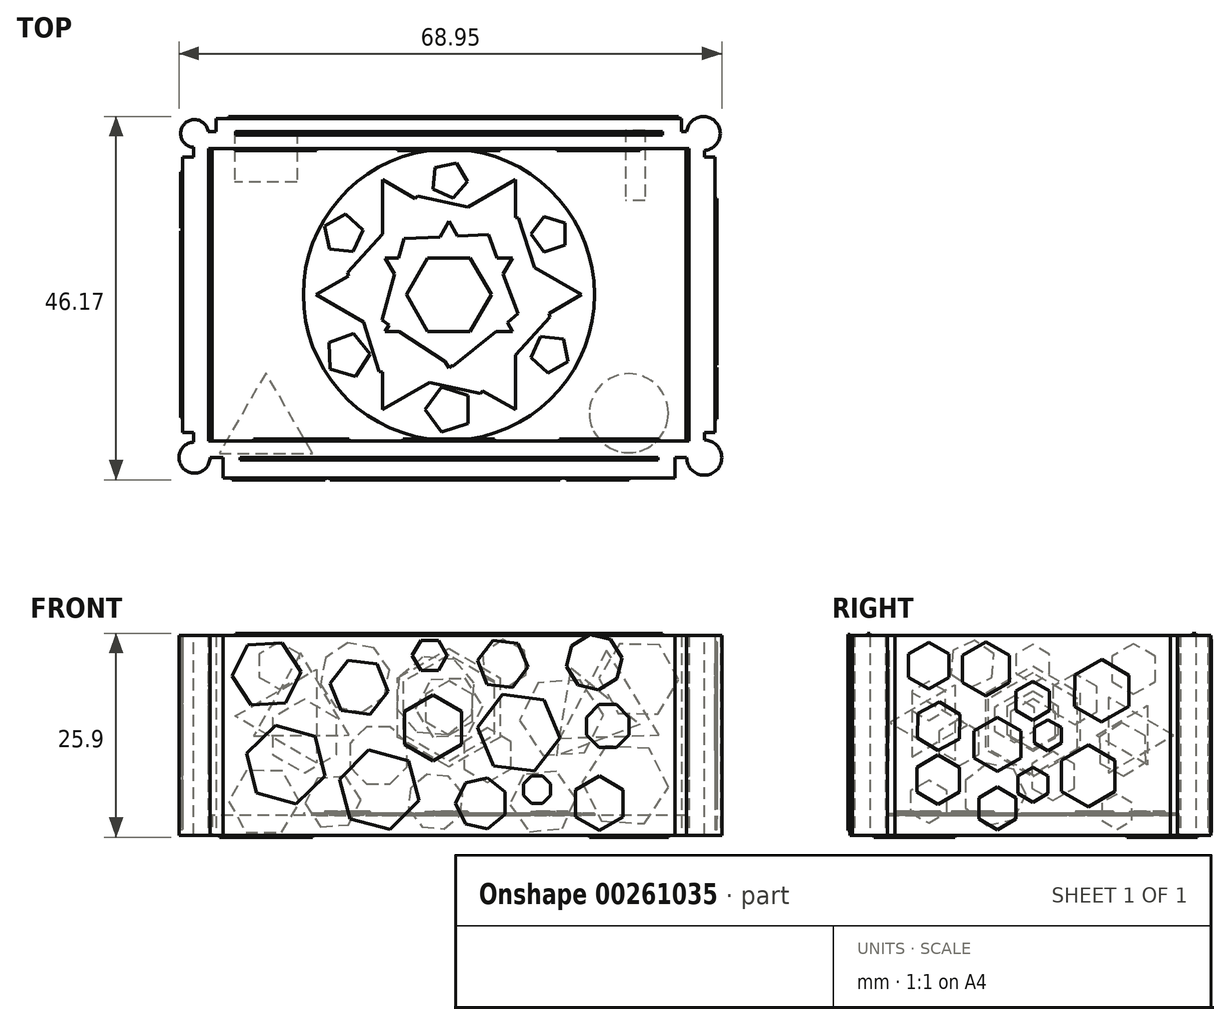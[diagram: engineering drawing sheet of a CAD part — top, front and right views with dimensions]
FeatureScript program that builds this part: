
annotation { "Feature Type Name" : "Feature", "Feature Type Description" : "" }
export const myFeature = defineFeature(function(context is Context, id is Id, definition is map)
    precondition{}
    {
        {
            var Q0;
            Q0=qCreatedBy(makeId("Top.planeOp"),FACE);
            var sketch = newSketch(context, id + "F0", { "sketchPlane" : qUnion([Q0])});
            skLineSegment(sketch, "E0.bottom", {"start": v(32.43, -20.7) * mm, "end": v(-32.43, -20.7) * mm});
            skLineSegment(sketch, "E0.top", {"start": v(32.43, 20.7) * mm, "end": v(-32.43, 20.7) * mm});
            skLineSegment(sketch, "E0.left", {"start": v(32.43, -20.7) * mm, "end": v(32.43, 20.7) * mm});
            skLineSegment(sketch, "E0.right", {"start": v(-32.43, -20.7) * mm, "end": v(-32.43, 20.7) * mm});
            skPoint(sketch, "E0.middle", {"position": v(0, 0) * mm});
            skLineSegment(sketch, "E1.bottom", {"start": v(30.51, -18.56) * mm, "end": v(-30.51, -18.56) * mm});
            skLineSegment(sketch, "E1.top", {"start": v(30.51, 18.56) * mm, "end": v(-30.51, 18.56) * mm});
            skLineSegment(sketch, "E1.left", {"start": v(30.51, -18.56) * mm, "end": v(30.51, 18.56) * mm});
            skLineSegment(sketch, "E1.right", {"start": v(-30.51, -18.56) * mm, "end": v(-30.51, 18.56) * mm});
            skSolve(sketch);
        }
        {
            var Q0;
            Q0=makeQuery(id+"F0.imprint","IMPRINT",FACE,{"disambiguationData":[TD([[makeQuery(id+"F0.imprint","IMPRINT",EDGE,{"derivedFrom":sQuery(id+"F0.wireOp",EDGE,"E0.bottom")}),-1.0]])]});
            extrude(context, id + "F1", {"entities" : qUnion([Q0]), "depth" : 25.4 * mm});
        }
        {
            var Q0;
            Q0=qCreatedBy(makeId("Top.planeOp"),FACE);
            var sketch = newSketch(context, id + "F2", { "sketchPlane" : qUnion([Q0])});
            skLineSegment(sketch, "E2.bottom", {"start": v(30.08, 18.56) * mm, "end": v(-30.08, 18.56) * mm});
            skLineSegment(sketch, "E2.top", {"start": v(30.08, -18.56) * mm, "end": v(-30.08, -18.56) * mm});
            skLineSegment(sketch, "E2.left", {"start": v(30.08, 18.56) * mm, "end": v(30.08, -18.56) * mm});
            skLineSegment(sketch, "E2.right", {"start": v(-30.08, 18.56) * mm, "end": v(-30.08, -18.56) * mm});
            skPoint(sketch, "E2.middle", {"position": v(0, 0) * mm});
            skSolve(sketch);
        }
        {
            var Q0;
            Q0=makeQuery(id+"F2.imprint","IMPRINT",FACE,{"disambiguationData":[TD([[makeQuery(id+"F2.imprint","IMPRINT",EDGE,{"derivedFrom":sQuery(id+"F2.wireOp",EDGE,"E2.bottom")}),1.0]])]});
            extrude(context, id + "F3", {"entities" : qUnion([Q0]), "operationType" : NewBodyOperationType.ADD, "depth" : 2.54 * mm});
        }
        {
            var Q0;
            Q0=qCreatedBy(makeId("Top.planeOp"),FACE);
            var sketch = newSketch(context, id + "F4", { "sketchPlane" : qUnion([Q0])});
            skCircle(sketch, "E3", {"center": v(32.43, -20.7) * mm, "radius": 2.23 * mm});
            skCircle(sketch, "E4", {"center": v(32.32, 20.48) * mm, "radius": 2.14 * mm});
            skCircle(sketch, "E5", {"center": v(-32.32, 20.48) * mm, "radius": 1.76 * mm});
            skCircle(sketch, "E6", {"center": v(-32.32, -20.7) * mm, "radius": 1.97 * mm});
            skSolve(sketch);
        }
        {
            var Q0;
            Q0 = qSketchRegion(id + "F4", true);
            extrude(context, id + "F5", {"entities" : qUnion([Q0]), "operationType" : NewBodyOperationType.ADD, "depth" : 25.4 * mm});
        }
        {
            var Q0;
            Q0=qCreatedBy(makeId("Top.planeOp"),FACE);
            var sketch = newSketch(context, id + "F6", { "sketchPlane" : qUnion([Q0])});
            skLineSegment(sketch, "E7.bottom", {"start": v(28.7, -23.26) * mm, "end": v(-28.7, -23.26) * mm});
            skLineSegment(sketch, "E7.top", {"start": v(28.7, -19.84) * mm, "end": v(-28.7, -19.84) * mm});
            skLineSegment(sketch, "E7.left", {"start": v(28.7, -23.26) * mm, "end": v(28.7, -19.84) * mm});
            skLineSegment(sketch, "E7.right", {"start": v(-28.7, -23.26) * mm, "end": v(-28.7, -19.84) * mm});
            skPoint(sketch, "E7.middle", {"position": v(0, -21.55) * mm});
            skLineSegment(sketch, "E8.bottom", {"start": v(29.55, 18.99) * mm, "end": v(-29.55, 18.99) * mm});
            skLineSegment(sketch, "E8.top", {"start": v(29.55, 22.4) * mm, "end": v(-29.55, 22.4) * mm});
            skLineSegment(sketch, "E8.left", {"start": v(29.55, 18.99) * mm, "end": v(29.55, 22.4) * mm});
            skLineSegment(sketch, "E8.right", {"start": v(-29.55, 18.99) * mm, "end": v(-29.55, 22.4) * mm});
            skPoint(sketch, "E8.middle", {"position": v(0, 20.7) * mm});
            skLineSegment(sketch, "E9.bottom", {"start": v(-31.26, -17.5) * mm, "end": v(-33.82, -17.5) * mm});
            skLineSegment(sketch, "E9.top", {"start": v(-31.26, 17.5) * mm, "end": v(-33.82, 17.5) * mm});
            skLineSegment(sketch, "E9.left", {"start": v(-31.26, -17.5) * mm, "end": v(-31.26, 17.5) * mm});
            skLineSegment(sketch, "E9.right", {"start": v(-33.82, -17.5) * mm, "end": v(-33.82, 17.5) * mm});
            skPoint(sketch, "E9.middle", {"position": v(-32.54, 0) * mm});
            skLineSegment(sketch, "E10.bottom", {"start": v(33.82, -17.5) * mm, "end": v(31.26, -17.5) * mm});
            skLineSegment(sketch, "E10.top", {"start": v(33.82, 17.5) * mm, "end": v(31.26, 17.5) * mm});
            skLineSegment(sketch, "E10.left", {"start": v(33.82, -17.5) * mm, "end": v(33.82, 17.5) * mm});
            skLineSegment(sketch, "E10.right", {"start": v(31.26, -17.5) * mm, "end": v(31.26, 17.5) * mm});
            skPoint(sketch, "E10.middle", {"position": v(32.54, 0) * mm});
            skSolve(sketch);
        }
        {
            var Q0;
            Q0 = qSketchRegion(id + "F6", true);
            extrude(context, id + "F7", {"entities" : qUnion([Q0]), "operationType" : NewBodyOperationType.ADD, "depth" : 25.4 * mm});
        }
        {
            var Q0;
            Q0=makeQuery(id+"F7.opExtrude","SWEPT_FACE",FACE,{"disambiguationData":[OSD([sQuery(id+"F6.wireOp",EDGE,"E7.bottom")])]});
            var sketch = newSketch(context, id + "F8", { "sketchPlane" : qUnion([Q0])});
            skCircle(sketch, "E11.cCircle", {"center": v(-23.15, 20.48) * mm, "radius": 3.82 * mm, "construction": true});
            skLineSegment(sketch, "E11.0", {"start": v(-18.75, 20.75) * mm, "end": v(-20.72, 16.8) * mm});
            skLineSegment(sketch, "E11.1", {"start": v(-20.72, 16.8) * mm, "end": v(-25.12, 16.54) * mm});
            skLineSegment(sketch, "E11.2", {"start": v(-25.12, 16.54) * mm, "end": v(-27.55, 20.22) * mm});
            skLineSegment(sketch, "E11.3", {"start": v(-27.55, 20.22) * mm, "end": v(-25.58, 24.16) * mm});
            skLineSegment(sketch, "E11.4", {"start": v(-25.58, 24.16) * mm, "end": v(-21.18, 24.42) * mm});
            skLineSegment(sketch, "E11.5", {"start": v(-21.18, 24.42) * mm, "end": v(-18.75, 20.75) * mm});
            skPoint(sketch, "E11.0.midPoint", {"position": v(-19.74, 18.78) * mm});
            skCircle(sketch, "E12.cCircle", {"center": v(-20.72, 8.96) * mm, "radius": 4.47 * mm, "construction": true});
            skLineSegment(sketch, "E12.0", {"start": v(-15.75, 7.56) * mm, "end": v(-19.45, 3.96) * mm});
            skLineSegment(sketch, "E12.1", {"start": v(-19.45, 3.96) * mm, "end": v(-24.42, 5.36) * mm});
            skLineSegment(sketch, "E12.2", {"start": v(-24.42, 5.36) * mm, "end": v(-25.69, 10.36) * mm});
            skLineSegment(sketch, "E12.3", {"start": v(-25.69, 10.36) * mm, "end": v(-22, 13.96) * mm});
            skLineSegment(sketch, "E12.4", {"start": v(-22, 13.96) * mm, "end": v(-17.03, 12.56) * mm});
            skLineSegment(sketch, "E12.5", {"start": v(-17.03, 12.56) * mm, "end": v(-15.75, 7.56) * mm});
            skPoint(sketch, "E12.0.midPoint", {"position": v(-17.6, 5.76) * mm});
            skCircle(sketch, "E13.cCircle", {"center": v(-11.41, 18.78) * mm, "radius": 3.23 * mm, "construction": true});
            skLineSegment(sketch, "E13.0", {"start": v(-7.72, 18.28) * mm, "end": v(-10, 15.33) * mm});
            skLineSegment(sketch, "E13.1", {"start": v(-10, 15.33) * mm, "end": v(-13.7, 15.82) * mm});
            skLineSegment(sketch, "E13.2", {"start": v(-13.7, 15.82) * mm, "end": v(-15.11, 19.27) * mm});
            skLineSegment(sketch, "E13.3", {"start": v(-15.11, 19.27) * mm, "end": v(-12.84, 22.22) * mm});
            skLineSegment(sketch, "E13.4", {"start": v(-12.84, 22.22) * mm, "end": v(-9.14, 21.73) * mm});
            skLineSegment(sketch, "E13.5", {"start": v(-9.14, 21.73) * mm, "end": v(-7.72, 18.28) * mm});
            skPoint(sketch, "E13.0.midPoint", {"position": v(-8.85, 16.8) * mm});
            skCircle(sketch, "E14.cCircle", {"center": v(-8.85, 5.76) * mm, "radius": 4.53 * mm, "construction": true});
            skLineSegment(sketch, "E14.0", {"start": v(-3.8, 4.4) * mm, "end": v(-7.5, 0.71) * mm});
            skLineSegment(sketch, "E14.1", {"start": v(-7.5, 0.71) * mm, "end": v(-12.55, 2.07) * mm});
            skLineSegment(sketch, "E14.2", {"start": v(-12.55, 2.07) * mm, "end": v(-13.9, 7.11) * mm});
            skLineSegment(sketch, "E14.3", {"start": v(-13.9, 7.11) * mm, "end": v(-10.2, 10.8) * mm});
            skLineSegment(sketch, "E14.4", {"start": v(-10.2, 10.8) * mm, "end": v(-5.16, 9.46) * mm});
            skLineSegment(sketch, "E14.5", {"start": v(-5.16, 9.46) * mm, "end": v(-3.8, 4.4) * mm});
            skPoint(sketch, "E14.0.midPoint", {"position": v(-5.65, 2.56) * mm});
            skCircle(sketch, "E15.cCircle", {"center": v(-2.03, 13.66) * mm, "radius": 3.63 * mm, "construction": true});
            skLineSegment(sketch, "E15.0", {"start": v(1.6, 15.75) * mm, "end": v(1.6, 11.56) * mm});
            skLineSegment(sketch, "E15.1", {"start": v(1.6, 11.56) * mm, "end": v(-2.03, 9.47) * mm});
            skLineSegment(sketch, "E15.2", {"start": v(-2.03, 9.47) * mm, "end": v(-5.65, 11.56) * mm});
            skLineSegment(sketch, "E15.3", {"start": v(-5.65, 11.56) * mm, "end": v(-5.65, 15.75) * mm});
            skLineSegment(sketch, "E15.4", {"start": v(-5.65, 15.75) * mm, "end": v(-2.03, 17.84) * mm});
            skLineSegment(sketch, "E15.5", {"start": v(-2.03, 17.84) * mm, "end": v(1.6, 15.75) * mm});
            skPoint(sketch, "E15.0.midPoint", {"position": v(1.6, 13.66) * mm});
            skCircle(sketch, "E16.cCircle", {"center": v(-2.45, 22.83) * mm, "radius": 1.92 * mm, "construction": true});
            skLineSegment(sketch, "E16.0", {"start": v(-1.34, 20.9) * mm, "end": v(-3.56, 20.9) * mm});
            skLineSegment(sketch, "E16.1", {"start": v(-3.56, 20.9) * mm, "end": v(-4.67, 22.83) * mm});
            skLineSegment(sketch, "E16.2", {"start": v(-4.67, 22.83) * mm, "end": v(-3.56, 24.75) * mm});
            skLineSegment(sketch, "E16.3", {"start": v(-3.56, 24.75) * mm, "end": v(-1.34, 24.75) * mm});
            skLineSegment(sketch, "E16.4", {"start": v(-1.34, 24.75) * mm, "end": v(-0.24, 22.83) * mm});
            skLineSegment(sketch, "E16.5", {"start": v(-0.24, 22.83) * mm, "end": v(-1.34, 20.9) * mm});
            skPoint(sketch, "E16.0.midPoint", {"position": v(-2.45, 20.9) * mm});
            skCircle(sketch, "E17.cCircle", {"center": v(4.16, 4.05) * mm, "radius": 2.99 * mm, "construction": true});
            skLineSegment(sketch, "E17.0", {"start": v(7.15, 5.5) * mm, "end": v(7.15, 2.62) * mm});
            skLineSegment(sketch, "E17.1", {"start": v(7.15, 2.62) * mm, "end": v(4.9, 0.82) * mm});
            skLineSegment(sketch, "E17.2", {"start": v(4.9, 0.82) * mm, "end": v(2.1, 1.46) * mm});
            skLineSegment(sketch, "E17.3", {"start": v(2.1, 1.46) * mm, "end": v(0.85, 4.05) * mm});
            skLineSegment(sketch, "E17.4", {"start": v(0.85, 4.05) * mm, "end": v(2.1, 6.65) * mm});
            skLineSegment(sketch, "E17.5", {"start": v(2.1, 6.65) * mm, "end": v(4.9, 7.29) * mm});
            skLineSegment(sketch, "E17.6", {"start": v(4.9, 7.29) * mm, "end": v(7.15, 5.5) * mm});
            skPoint(sketch, "E17.0.midPoint", {"position": v(7.15, 4.05) * mm});
            skCircle(sketch, "E18.cCircle", {"center": v(8.85, 13.01) * mm, "radius": 4.57 * mm, "construction": true});
            skLineSegment(sketch, "E18.0", {"start": v(14.08, 12.34) * mm, "end": v(10.88, 8.15) * mm});
            skLineSegment(sketch, "E18.1", {"start": v(10.88, 8.15) * mm, "end": v(5.65, 8.83) * mm});
            skLineSegment(sketch, "E18.2", {"start": v(5.65, 8.83) * mm, "end": v(3.63, 13.7) * mm});
            skLineSegment(sketch, "E18.3", {"start": v(3.63, 13.7) * mm, "end": v(6.83, 17.88) * mm});
            skLineSegment(sketch, "E18.4", {"start": v(6.83, 17.88) * mm, "end": v(12.06, 17.2) * mm});
            skLineSegment(sketch, "E18.5", {"start": v(12.06, 17.2) * mm, "end": v(14.08, 12.34) * mm});
            skPoint(sketch, "E18.0.midPoint", {"position": v(12.48, 10.24) * mm});
            skCircle(sketch, "E19.cCircle", {"center": v(6.83, 21.76) * mm, "radius": 2.82 * mm, "construction": true});
            skLineSegment(sketch, "E19.0", {"start": v(10.05, 21.35) * mm, "end": v(8.08, 18.76) * mm});
            skLineSegment(sketch, "E19.1", {"start": v(8.08, 18.76) * mm, "end": v(4.86, 19.18) * mm});
            skLineSegment(sketch, "E19.2", {"start": v(4.86, 19.18) * mm, "end": v(3.6, 22.18) * mm});
            skLineSegment(sketch, "E19.3", {"start": v(3.6, 22.18) * mm, "end": v(5.58, 24.76) * mm});
            skLineSegment(sketch, "E19.4", {"start": v(5.58, 24.76) * mm, "end": v(8.8, 24.35) * mm});
            skLineSegment(sketch, "E19.5", {"start": v(8.8, 24.35) * mm, "end": v(10.05, 21.35) * mm});
            skPoint(sketch, "E19.0.midPoint", {"position": v(9.07, 20.06) * mm});
            skCircle(sketch, "E20.cCircle", {"center": v(19.1, 4.05) * mm, "radius": 2.99 * mm, "construction": true});
            skLineSegment(sketch, "E20.0", {"start": v(22.08, 5.78) * mm, "end": v(22.08, 2.33) * mm});
            skLineSegment(sketch, "E20.1", {"start": v(22.08, 2.33) * mm, "end": v(19.1, 0.6) * mm});
            skLineSegment(sketch, "E20.2", {"start": v(19.1, 0.6) * mm, "end": v(16.1, 2.33) * mm});
            skLineSegment(sketch, "E20.3", {"start": v(16.1, 2.33) * mm, "end": v(16.1, 5.78) * mm});
            skLineSegment(sketch, "E20.4", {"start": v(16.1, 5.78) * mm, "end": v(19.1, 7.5) * mm});
            skLineSegment(sketch, "E20.5", {"start": v(19.1, 7.5) * mm, "end": v(22.08, 5.78) * mm});
            skPoint(sketch, "E20.0.midPoint", {"position": v(22.08, 4.05) * mm});
            skCircle(sketch, "E21.cCircle", {"center": v(11.2, 5.78) * mm, "radius": 1.72 * mm, "construction": true});
            skLineSegment(sketch, "E21.0", {"start": v(11.92, 4.05) * mm, "end": v(10.49, 4.05) * mm});
            skLineSegment(sketch, "E21.1", {"start": v(10.49, 4.05) * mm, "end": v(9.48, 5.06) * mm});
            skLineSegment(sketch, "E21.2", {"start": v(9.48, 5.06) * mm, "end": v(9.48, 6.5) * mm});
            skLineSegment(sketch, "E21.3", {"start": v(9.48, 6.5) * mm, "end": v(10.49, 7.5) * mm});
            skLineSegment(sketch, "E21.4", {"start": v(10.49, 7.5) * mm, "end": v(11.92, 7.5) * mm});
            skLineSegment(sketch, "E21.5", {"start": v(11.92, 7.5) * mm, "end": v(12.93, 6.5) * mm});
            skLineSegment(sketch, "E21.6", {"start": v(12.93, 6.5) * mm, "end": v(12.93, 5.06) * mm});
            skLineSegment(sketch, "E21.7", {"start": v(12.93, 5.06) * mm, "end": v(11.92, 4.05) * mm});
            skPoint(sketch, "E21.0.midPoint", {"position": v(11.2, 4.05) * mm});
            skCircle(sketch, "E22.cCircle", {"center": v(18.46, 21.98) * mm, "radius": 3.28 * mm, "construction": true});
            skLineSegment(sketch, "E22.0", {"start": v(21.32, 19.88) * mm, "end": v(19, 18.47) * mm});
            skLineSegment(sketch, "E22.1", {"start": v(19, 18.47) * mm, "end": v(16.36, 19.1) * mm});
            skLineSegment(sketch, "E22.2", {"start": v(16.36, 19.1) * mm, "end": v(14.95, 21.43) * mm});
            skLineSegment(sketch, "E22.3", {"start": v(14.95, 21.43) * mm, "end": v(15.59, 24.07) * mm});
            skLineSegment(sketch, "E22.4", {"start": v(15.59, 24.07) * mm, "end": v(17.9, 25.48) * mm});
            skLineSegment(sketch, "E22.5", {"start": v(17.9, 25.48) * mm, "end": v(20.55, 24.84) * mm});
            skLineSegment(sketch, "E22.6", {"start": v(20.55, 24.84) * mm, "end": v(21.96, 22.52) * mm});
            skLineSegment(sketch, "E22.7", {"start": v(21.96, 22.52) * mm, "end": v(21.32, 19.88) * mm});
            skPoint(sketch, "E22.0.midPoint", {"position": v(20.16, 19.18) * mm});
            skCircle(sketch, "E23.cCircle", {"center": v(20.16, 13.87) * mm, "radius": 2.72 * mm, "construction": true});
            skLineSegment(sketch, "E23.0", {"start": v(22.88, 12.74) * mm, "end": v(21.29, 11.15) * mm});
            skLineSegment(sketch, "E23.1", {"start": v(21.29, 11.15) * mm, "end": v(19.04, 11.15) * mm});
            skLineSegment(sketch, "E23.2", {"start": v(19.04, 11.15) * mm, "end": v(17.45, 12.74) * mm});
            skLineSegment(sketch, "E23.3", {"start": v(17.45, 12.74) * mm, "end": v(17.45, 15) * mm});
            skLineSegment(sketch, "E23.4", {"start": v(17.45, 15) * mm, "end": v(19.04, 16.58) * mm});
            skLineSegment(sketch, "E23.5", {"start": v(19.04, 16.58) * mm, "end": v(21.29, 16.58) * mm});
            skLineSegment(sketch, "E23.6", {"start": v(21.29, 16.58) * mm, "end": v(22.88, 15) * mm});
            skLineSegment(sketch, "E23.7", {"start": v(22.88, 15) * mm, "end": v(22.88, 12.74) * mm});
            skPoint(sketch, "E23.0.midPoint", {"position": v(22.08, 11.95) * mm});
            skSolve(sketch);
        }
        {
            var Q0;
            Q0 = qSketchRegion(id + "F8", true);
            extrude(context, id + "F9", {"entities" : qUnion([Q0]), "operationType" : NewBodyOperationType.ADD, "depth" : 0.25 * mm});
        }
        {
            var Q0;
            Q0=makeQuery(id+"F7.opExtrude","SWEPT_FACE",FACE,{"disambiguationData":[OSD([sQuery(id+"F6.wireOp",EDGE,"E8.top")])]});
            var sketch = newSketch(context, id + "F10", { "sketchPlane" : qUnion([Q0])});
            skCircle(sketch, "E24.cCircle", {"center": v(-24.1, 19.84) * mm, "radius": 4.4 * mm, "construction": true});
            skLineSegment(sketch, "E24.0", {"start": v(-19.04, 19.93) * mm, "end": v(-21.5, 15.5) * mm});
            skLineSegment(sketch, "E24.1", {"start": v(-21.5, 15.5) * mm, "end": v(-26.57, 15.4) * mm});
            skLineSegment(sketch, "E24.2", {"start": v(-26.57, 15.4) * mm, "end": v(-29.18, 19.76) * mm});
            skLineSegment(sketch, "E24.3", {"start": v(-29.18, 19.76) * mm, "end": v(-26.72, 24.2) * mm});
            skLineSegment(sketch, "E24.4", {"start": v(-26.72, 24.2) * mm, "end": v(-21.65, 24.28) * mm});
            skLineSegment(sketch, "E24.5", {"start": v(-21.65, 24.28) * mm, "end": v(-19.04, 19.93) * mm});
            skPoint(sketch, "E24.0.midPoint", {"position": v(-20.27, 17.7) * mm});
            skCircle(sketch, "E25.cCircle", {"center": v(-22.4, 6.4) * mm, "radius": 4.77 * mm, "construction": true});
            skLineSegment(sketch, "E25.0", {"start": v(-16.9, 6.73) * mm, "end": v(-19.37, 1.8) * mm});
            skLineSegment(sketch, "E25.1", {"start": v(-19.37, 1.8) * mm, "end": v(-24.87, 1.47) * mm});
            skLineSegment(sketch, "E25.2", {"start": v(-24.87, 1.47) * mm, "end": v(-27.9, 6.07) * mm});
            skLineSegment(sketch, "E25.3", {"start": v(-27.9, 6.07) * mm, "end": v(-25.44, 11) * mm});
            skLineSegment(sketch, "E25.4", {"start": v(-25.44, 11) * mm, "end": v(-19.94, 11.33) * mm});
            skLineSegment(sketch, "E25.5", {"start": v(-19.94, 11.33) * mm, "end": v(-16.9, 6.73) * mm});
            skPoint(sketch, "E25.0.midPoint", {"position": v(-18.14, 4.27) * mm});
            skCircle(sketch, "E26.cCircle", {"center": v(-14.3, 14.94) * mm, "radius": 4.62 * mm, "construction": true});
            skLineSegment(sketch, "E26.0", {"start": v(-8.98, 14.6) * mm, "end": v(-11.93, 10.16) * mm});
            skLineSegment(sketch, "E26.1", {"start": v(-11.93, 10.16) * mm, "end": v(-17.25, 10.5) * mm});
            skLineSegment(sketch, "E26.2", {"start": v(-17.25, 10.5) * mm, "end": v(-19.61, 15.28) * mm});
            skLineSegment(sketch, "E26.3", {"start": v(-19.61, 15.28) * mm, "end": v(-16.66, 19.71) * mm});
            skLineSegment(sketch, "E26.4", {"start": v(-16.66, 19.71) * mm, "end": v(-11.34, 19.37) * mm});
            skLineSegment(sketch, "E26.5", {"start": v(-11.34, 19.37) * mm, "end": v(-8.98, 14.6) * mm});
            skPoint(sketch, "E26.0.midPoint", {"position": v(-10.45, 12.37) * mm});
            skCircle(sketch, "E27.cCircle", {"center": v(-11.93, 4.27) * mm, "radius": 3.65 * mm, "construction": true});
            skLineSegment(sketch, "E27.0", {"start": v(-7.74, 3.84) * mm, "end": v(-10.2, 0.43) * mm});
            skLineSegment(sketch, "E27.1", {"start": v(-10.2, 0.43) * mm, "end": v(-14.4, 0.85) * mm});
            skLineSegment(sketch, "E27.2", {"start": v(-14.4, 0.85) * mm, "end": v(-16.12, 4.7) * mm});
            skLineSegment(sketch, "E27.3", {"start": v(-16.12, 4.7) * mm, "end": v(-13.66, 8.1) * mm});
            skLineSegment(sketch, "E27.4", {"start": v(-13.66, 8.1) * mm, "end": v(-9.47, 7.68) * mm});
            skLineSegment(sketch, "E27.5", {"start": v(-9.47, 7.68) * mm, "end": v(-7.74, 3.84) * mm});
            skPoint(sketch, "E27.0.midPoint", {"position": v(-8.98, 2.13) * mm});
            skCircle(sketch, "E28.cCircle", {"center": v(-4.9, 10.16) * mm, "radius": 2.99 * mm, "construction": true});
            skLineSegment(sketch, "E28.0", {"start": v(-1.92, 11.88) * mm, "end": v(-1.92, 8.43) * mm});
            skLineSegment(sketch, "E28.1", {"start": v(-1.92, 8.43) * mm, "end": v(-4.9, 6.7) * mm});
            skLineSegment(sketch, "E28.2", {"start": v(-4.9, 6.7) * mm, "end": v(-7.9, 8.43) * mm});
            skLineSegment(sketch, "E28.3", {"start": v(-7.9, 8.43) * mm, "end": v(-7.9, 11.88) * mm});
            skLineSegment(sketch, "E28.4", {"start": v(-7.9, 11.88) * mm, "end": v(-4.9, 13.6) * mm});
            skLineSegment(sketch, "E28.5", {"start": v(-4.9, 13.6) * mm, "end": v(-1.92, 11.88) * mm});
            skPoint(sketch, "E28.0.midPoint", {"position": v(-1.92, 10.16) * mm});
            skCircle(sketch, "E29.cCircle", {"center": v(-7.04, 21.76) * mm, "radius": 2.67 * mm, "construction": true});
            skLineSegment(sketch, "E29.0", {"start": v(-4.48, 20.05) * mm, "end": v(-7.24, 18.69) * mm});
            skLineSegment(sketch, "E29.1", {"start": v(-7.24, 18.69) * mm, "end": v(-9.8, 20.4) * mm});
            skLineSegment(sketch, "E29.2", {"start": v(-9.8, 20.4) * mm, "end": v(-9.6, 23.47) * mm});
            skLineSegment(sketch, "E29.3", {"start": v(-9.6, 23.47) * mm, "end": v(-6.84, 24.84) * mm});
            skLineSegment(sketch, "E29.4", {"start": v(-6.84, 24.84) * mm, "end": v(-4.28, 23.13) * mm});
            skLineSegment(sketch, "E29.5", {"start": v(-4.28, 23.13) * mm, "end": v(-4.48, 20.05) * mm});
            skPoint(sketch, "E29.0.midPoint", {"position": v(-5.86, 19.37) * mm});
            skCircle(sketch, "E30.cCircle", {"center": v(1.7, 17.7) * mm, "radius": 4.78 * mm, "construction": true});
            skLineSegment(sketch, "E30.0", {"start": v(6.62, 16.1) * mm, "end": v(4.04, 13.09) * mm});
            skLineSegment(sketch, "E30.1", {"start": v(4.04, 13.09) * mm, "end": v(0.1, 12.8) * mm});
            skLineSegment(sketch, "E30.2", {"start": v(0.1, 12.8) * mm, "end": v(-2.91, 15.37) * mm});
            skLineSegment(sketch, "E30.3", {"start": v(-2.91, 15.37) * mm, "end": v(-3.21, 19.32) * mm});
            skLineSegment(sketch, "E30.4", {"start": v(-3.21, 19.32) * mm, "end": v(-0.63, 22.33) * mm});
            skLineSegment(sketch, "E30.5", {"start": v(-0.63, 22.33) * mm, "end": v(3.32, 22.63) * mm});
            skLineSegment(sketch, "E30.6", {"start": v(3.32, 22.63) * mm, "end": v(6.33, 20.05) * mm});
            skLineSegment(sketch, "E30.7", {"start": v(6.33, 20.05) * mm, "end": v(6.62, 16.1) * mm});
            skPoint(sketch, "E30.0.midPoint", {"position": v(5.33, 14.6) * mm});
            skCircle(sketch, "E31.cCircle", {"center": v(1.7, 4.27) * mm, "radius": 3.33 * mm, "construction": true});
            skLineSegment(sketch, "E31.0", {"start": v(5.15, 3.2) * mm, "end": v(3.38, 1.07) * mm});
            skLineSegment(sketch, "E31.1", {"start": v(3.38, 1.07) * mm, "end": v(0.63, 0.82) * mm});
            skLineSegment(sketch, "E31.2", {"start": v(0.63, 0.82) * mm, "end": v(-1.49, 2.6) * mm});
            skLineSegment(sketch, "E31.3", {"start": v(-1.49, 2.6) * mm, "end": v(-1.74, 5.34) * mm});
            skLineSegment(sketch, "E31.4", {"start": v(-1.74, 5.34) * mm, "end": v(0.03, 7.46) * mm});
            skLineSegment(sketch, "E31.5", {"start": v(0.03, 7.46) * mm, "end": v(2.78, 7.71) * mm});
            skLineSegment(sketch, "E31.6", {"start": v(2.78, 7.71) * mm, "end": v(4.9, 5.94) * mm});
            skLineSegment(sketch, "E31.7", {"start": v(4.9, 5.94) * mm, "end": v(5.15, 3.2) * mm});
            skPoint(sketch, "E31.0.midPoint", {"position": v(4.27, 2.13) * mm});
            skCircle(sketch, "E32.cCircle", {"center": v(8.96, 10.16) * mm, "radius": 3.63 * mm, "construction": true});
            skLineSegment(sketch, "E32.0", {"start": v(12.59, 11.66) * mm, "end": v(12.59, 8.66) * mm});
            skLineSegment(sketch, "E32.1", {"start": v(12.59, 8.66) * mm, "end": v(10.46, 6.53) * mm});
            skLineSegment(sketch, "E32.2", {"start": v(10.46, 6.53) * mm, "end": v(7.46, 6.53) * mm});
            skLineSegment(sketch, "E32.3", {"start": v(7.46, 6.53) * mm, "end": v(5.33, 8.66) * mm});
            skLineSegment(sketch, "E32.4", {"start": v(5.33, 8.66) * mm, "end": v(5.33, 11.66) * mm});
            skLineSegment(sketch, "E32.5", {"start": v(5.33, 11.66) * mm, "end": v(7.46, 13.78) * mm});
            skLineSegment(sketch, "E32.6", {"start": v(7.46, 13.78) * mm, "end": v(10.46, 13.78) * mm});
            skLineSegment(sketch, "E32.7", {"start": v(10.46, 13.78) * mm, "end": v(12.59, 11.66) * mm});
            skPoint(sketch, "E32.0.midPoint", {"position": v(12.59, 10.16) * mm});
            skCircle(sketch, "E33.cCircle", {"center": v(11.95, 20.05) * mm, "radius": 4.14 * mm, "construction": true});
            skLineSegment(sketch, "E33.0", {"start": v(16.33, 19.12) * mm, "end": v(14.4, 16.3) * mm});
            skLineSegment(sketch, "E33.1", {"start": v(14.4, 16.3) * mm, "end": v(11.03, 15.66) * mm});
            skLineSegment(sketch, "E33.2", {"start": v(11.03, 15.66) * mm, "end": v(8.2, 17.6) * mm});
            skLineSegment(sketch, "E33.3", {"start": v(8.2, 17.6) * mm, "end": v(7.57, 20.97) * mm});
            skLineSegment(sketch, "E33.4", {"start": v(7.57, 20.97) * mm, "end": v(9.5, 23.8) * mm});
            skLineSegment(sketch, "E33.5", {"start": v(9.5, 23.8) * mm, "end": v(12.87, 24.43) * mm});
            skLineSegment(sketch, "E33.6", {"start": v(12.87, 24.43) * mm, "end": v(15.7, 22.5) * mm});
            skLineSegment(sketch, "E33.7", {"start": v(15.7, 22.5) * mm, "end": v(16.33, 19.12) * mm});
            skPoint(sketch, "E33.0.midPoint", {"position": v(15.36, 17.7) * mm});
            skCircle(sketch, "E34.cCircle", {"center": v(14.72, 4.27) * mm, "radius": 3.08 * mm, "construction": true});
            skLineSegment(sketch, "E34.0", {"start": v(18.27, 4.04) * mm, "end": v(16.3, 1.08) * mm});
            skLineSegment(sketch, "E34.1", {"start": v(16.3, 1.08) * mm, "end": v(12.75, 1.31) * mm});
            skLineSegment(sketch, "E34.2", {"start": v(12.75, 1.31) * mm, "end": v(11.18, 4.5) * mm});
            skLineSegment(sketch, "E34.3", {"start": v(11.18, 4.5) * mm, "end": v(13.15, 7.45) * mm});
            skLineSegment(sketch, "E34.4", {"start": v(13.15, 7.45) * mm, "end": v(16.7, 7.22) * mm});
            skLineSegment(sketch, "E34.5", {"start": v(16.7, 7.22) * mm, "end": v(18.27, 4.04) * mm});
            skPoint(sketch, "E34.0.midPoint", {"position": v(17.28, 2.56) * mm});
            skCircle(sketch, "E35.cCircle", {"center": v(18.35, 12.59) * mm, "radius": 4.05 * mm, "construction": true});
            skLineSegment(sketch, "E35.0", {"start": v(22.4, 14.93) * mm, "end": v(22.4, 10.25) * mm});
            skLineSegment(sketch, "E35.1", {"start": v(22.4, 10.25) * mm, "end": v(18.35, 7.9) * mm});
            skLineSegment(sketch, "E35.2", {"start": v(18.35, 7.9) * mm, "end": v(14.3, 10.25) * mm});
            skLineSegment(sketch, "E35.3", {"start": v(14.3, 10.25) * mm, "end": v(14.3, 14.93) * mm});
            skLineSegment(sketch, "E35.4", {"start": v(14.3, 14.93) * mm, "end": v(18.35, 17.27) * mm});
            skLineSegment(sketch, "E35.5", {"start": v(18.35, 17.27) * mm, "end": v(22.4, 14.93) * mm});
            skPoint(sketch, "E35.0.midPoint", {"position": v(22.4, 12.59) * mm});
            skCircle(sketch, "E36.cCircle", {"center": v(21.55, 21.55) * mm, "radius": 2.56 * mm, "construction": true});
            skLineSegment(sketch, "E36.0", {"start": v(24.1, 23.03) * mm, "end": v(24.1, 20.07) * mm});
            skLineSegment(sketch, "E36.1", {"start": v(24.1, 20.07) * mm, "end": v(21.55, 18.6) * mm});
            skLineSegment(sketch, "E36.2", {"start": v(21.55, 18.6) * mm, "end": v(18.99, 20.07) * mm});
            skLineSegment(sketch, "E36.3", {"start": v(18.99, 20.07) * mm, "end": v(18.99, 23.03) * mm});
            skLineSegment(sketch, "E36.4", {"start": v(18.99, 23.03) * mm, "end": v(21.55, 24.5) * mm});
            skLineSegment(sketch, "E36.5", {"start": v(21.55, 24.5) * mm, "end": v(24.1, 23.03) * mm});
            skPoint(sketch, "E36.0.midPoint", {"position": v(24.1, 21.55) * mm});
            skCircle(sketch, "E37.cCircle", {"center": v(23.47, 4.27) * mm, "radius": 3.92 * mm, "construction": true});
            skLineSegment(sketch, "E37.0", {"start": v(28, 4.32) * mm, "end": v(25.77, 0.38) * mm});
            skLineSegment(sketch, "E37.1", {"start": v(25.77, 0.38) * mm, "end": v(21.25, 0.33) * mm});
            skLineSegment(sketch, "E37.2", {"start": v(21.25, 0.33) * mm, "end": v(18.95, 4.22) * mm});
            skLineSegment(sketch, "E37.3", {"start": v(18.95, 4.22) * mm, "end": v(21.16, 8.16) * mm});
            skLineSegment(sketch, "E37.4", {"start": v(21.16, 8.16) * mm, "end": v(25.69, 8.2) * mm});
            skLineSegment(sketch, "E37.5", {"start": v(25.69, 8.2) * mm, "end": v(28, 4.32) * mm});
            skPoint(sketch, "E37.0.midPoint", {"position": v(26.88, 2.35) * mm});
            skSolve(sketch);
        }
        {
            var Q0;
            Q0 = qSketchRegion(id + "F10", true);
            extrude(context, id + "F11", {"entities" : qUnion([Q0]), "operationType" : NewBodyOperationType.ADD, "depth" : 0.25 * mm});
        }
        {
            var Q0;
            Q0=makeQuery(id+"F7.opExtrude","SWEPT_FACE",FACE,{"disambiguationData":[OSD([sQuery(id+"F6.wireOp",EDGE,"E10.left")])]});
            var sketch = newSketch(context, id + "F12", { "sketchPlane" : qUnion([Q0])});
            skCircle(sketch, "E38.cCircle", {"center": v(-13.23, 21.55) * mm, "radius": 2.56 * mm, "construction": true});
            skLineSegment(sketch, "E38.0", {"start": v(-10.67, 23.03) * mm, "end": v(-10.67, 20.07) * mm});
            skLineSegment(sketch, "E38.1", {"start": v(-10.67, 20.07) * mm, "end": v(-13.23, 18.6) * mm});
            skLineSegment(sketch, "E38.2", {"start": v(-13.23, 18.6) * mm, "end": v(-15.79, 20.07) * mm});
            skLineSegment(sketch, "E38.3", {"start": v(-15.79, 20.07) * mm, "end": v(-15.79, 23.03) * mm});
            skLineSegment(sketch, "E38.4", {"start": v(-15.79, 23.03) * mm, "end": v(-13.23, 24.5) * mm});
            skLineSegment(sketch, "E38.5", {"start": v(-13.23, 24.5) * mm, "end": v(-10.67, 23.03) * mm});
            skPoint(sketch, "E38.0.midPoint", {"position": v(-10.67, 21.55) * mm});
            skCircle(sketch, "E39.cCircle", {"center": v(-11.95, 13.87) * mm, "radius": 2.67 * mm, "construction": true});
            skPoint(sketch, "E39.cCircle.centerSnap0", {"position": v(-11.95, 19.33) * mm});
            skLineSegment(sketch, "E39.0", {"start": v(-9.31, 12.26) * mm, "end": v(-12.02, 10.78) * mm});
            skLineSegment(sketch, "E39.1", {"start": v(-12.02, 10.78) * mm, "end": v(-14.66, 12.4) * mm});
            skLineSegment(sketch, "E39.2", {"start": v(-14.66, 12.4) * mm, "end": v(-14.58, 15.48) * mm});
            skLineSegment(sketch, "E39.3", {"start": v(-14.58, 15.48) * mm, "end": v(-11.87, 16.95) * mm});
            skLineSegment(sketch, "E39.4", {"start": v(-11.87, 16.95) * mm, "end": v(-9.24, 15.35) * mm});
            skLineSegment(sketch, "E39.5", {"start": v(-9.24, 15.35) * mm, "end": v(-9.31, 12.26) * mm});
            skPoint(sketch, "E39.0.midPoint", {"position": v(-10.67, 11.52) * mm});
            skCircle(sketch, "E40.cCircle", {"center": v(-12.02, 7.04) * mm, "radius": 2.71 * mm, "construction": true});
            skLineSegment(sketch, "E40.0", {"start": v(-9.31, 8.6) * mm, "end": v(-9.31, 5.48) * mm});
            skLineSegment(sketch, "E40.1", {"start": v(-9.31, 5.48) * mm, "end": v(-12.02, 3.91) * mm});
            skLineSegment(sketch, "E40.2", {"start": v(-12.02, 3.91) * mm, "end": v(-14.73, 5.48) * mm});
            skLineSegment(sketch, "E40.3", {"start": v(-14.73, 5.48) * mm, "end": v(-14.73, 8.6) * mm});
            skLineSegment(sketch, "E40.4", {"start": v(-14.73, 8.6) * mm, "end": v(-12.02, 10.17) * mm});
            skLineSegment(sketch, "E40.5", {"start": v(-12.02, 10.17) * mm, "end": v(-9.31, 8.6) * mm});
            skPoint(sketch, "E40.0.midPoint", {"position": v(-9.31, 7.04) * mm});
            skCircle(sketch, "E41.cCircle", {"center": v(-5.97, 21.12) * mm, "radius": 2.99 * mm, "construction": true});
            skLineSegment(sketch, "E41.0", {"start": v(-2.99, 22.85) * mm, "end": v(-2.99, 19.4) * mm});
            skLineSegment(sketch, "E41.1", {"start": v(-2.99, 19.4) * mm, "end": v(-5.97, 17.67) * mm});
            skLineSegment(sketch, "E41.2", {"start": v(-5.97, 17.67) * mm, "end": v(-8.96, 19.4) * mm});
            skLineSegment(sketch, "E41.3", {"start": v(-8.96, 19.4) * mm, "end": v(-8.96, 22.85) * mm});
            skLineSegment(sketch, "E41.4", {"start": v(-8.96, 22.85) * mm, "end": v(-5.97, 24.57) * mm});
            skLineSegment(sketch, "E41.5", {"start": v(-5.97, 24.57) * mm, "end": v(-2.99, 22.85) * mm});
            skPoint(sketch, "E41.0.midPoint", {"position": v(-2.99, 21.12) * mm});
            skCircle(sketch, "E42.cCircle", {"center": v(-4.48, 11.52) * mm, "radius": 2.99 * mm, "construction": true});
            skPoint(sketch, "E42.cCircle.centerSnap0", {"position": v(-4.48, 18.54) * mm});
            skLineSegment(sketch, "E42.0", {"start": v(-1.5, 9.8) * mm, "end": v(-4.48, 8.07) * mm});
            skLineSegment(sketch, "E42.1", {"start": v(-4.48, 8.07) * mm, "end": v(-7.47, 9.8) * mm});
            skLineSegment(sketch, "E42.2", {"start": v(-7.47, 9.8) * mm, "end": v(-7.47, 13.25) * mm});
            skLineSegment(sketch, "E42.3", {"start": v(-7.47, 13.25) * mm, "end": v(-4.48, 14.97) * mm});
            skLineSegment(sketch, "E42.4", {"start": v(-4.48, 14.97) * mm, "end": v(-1.5, 13.25) * mm});
            skLineSegment(sketch, "E42.5", {"start": v(-1.5, 13.25) * mm, "end": v(-1.5, 9.8) * mm});
            skPoint(sketch, "E42.0.midPoint", {"position": v(-2.99, 8.93) * mm});
            skCircle(sketch, "E43.cCircle", {"center": v(-4.48, 3.41) * mm, "radius": 2.35 * mm, "construction": true});
            skLineSegment(sketch, "E43.0", {"start": v(-2.13, 4.77) * mm, "end": v(-2.13, 2.06) * mm});
            skLineSegment(sketch, "E43.1", {"start": v(-2.13, 2.06) * mm, "end": v(-4.48, 0.7) * mm});
            skLineSegment(sketch, "E43.2", {"start": v(-4.48, 0.7) * mm, "end": v(-6.83, 2.06) * mm});
            skLineSegment(sketch, "E43.3", {"start": v(-6.83, 2.06) * mm, "end": v(-6.83, 4.77) * mm});
            skLineSegment(sketch, "E43.4", {"start": v(-6.83, 4.77) * mm, "end": v(-4.48, 6.12) * mm});
            skLineSegment(sketch, "E43.5", {"start": v(-4.48, 6.12) * mm, "end": v(-2.13, 4.77) * mm});
            skPoint(sketch, "E43.0.midPoint", {"position": v(-2.13, 3.41) * mm});
            skCircle(sketch, "E44.cCircle", {"center": v(0, 17.07) * mm, "radius": 2.13 * mm, "construction": true});
            skLineSegment(sketch, "E44.0", {"start": v(2.13, 18.3) * mm, "end": v(2.13, 15.84) * mm});
            skLineSegment(sketch, "E44.1", {"start": v(2.13, 15.84) * mm, "end": v(0, 14.6) * mm});
            skLineSegment(sketch, "E44.2", {"start": v(0, 14.6) * mm, "end": v(-2.13, 15.84) * mm});
            skLineSegment(sketch, "E44.3", {"start": v(-2.13, 15.84) * mm, "end": v(-2.13, 18.3) * mm});
            skLineSegment(sketch, "E44.4", {"start": v(-2.13, 18.3) * mm, "end": v(0, 19.53) * mm});
            skLineSegment(sketch, "E44.5", {"start": v(0, 19.53) * mm, "end": v(2.13, 18.3) * mm});
            skPoint(sketch, "E44.0.midPoint", {"position": v(2.13, 17.07) * mm});
            skCircle(sketch, "E45.cCircle", {"center": v(0, 6.4) * mm, "radius": 1.92 * mm, "construction": true});
            skLineSegment(sketch, "E45.0", {"start": v(1.92, 7.5) * mm, "end": v(1.92, 5.3) * mm});
            skLineSegment(sketch, "E45.1", {"start": v(1.92, 5.3) * mm, "end": v(0, 4.18) * mm});
            skLineSegment(sketch, "E45.2", {"start": v(0, 4.18) * mm, "end": v(-1.92, 5.3) * mm});
            skLineSegment(sketch, "E45.3", {"start": v(-1.92, 5.3) * mm, "end": v(-1.92, 7.5) * mm});
            skLineSegment(sketch, "E45.4", {"start": v(-1.92, 7.5) * mm, "end": v(0, 8.62) * mm});
            skLineSegment(sketch, "E45.5", {"start": v(0, 8.62) * mm, "end": v(1.92, 7.5) * mm});
            skPoint(sketch, "E45.0.midPoint", {"position": v(1.92, 6.4) * mm});
            skCircle(sketch, "E46.cCircle", {"center": v(1.92, 12.7) * mm, "radius": 1.7 * mm, "construction": true});
            skPoint(sketch, "E46.cCircle.centerSnap0", {"position": v(17.5, 12.7) * mm});
            skLineSegment(sketch, "E46.0", {"start": v(3.63, 13.69) * mm, "end": v(3.63, 11.71) * mm});
            skLineSegment(sketch, "E46.1", {"start": v(3.63, 11.71) * mm, "end": v(1.92, 10.73) * mm});
            skLineSegment(sketch, "E46.2", {"start": v(1.92, 10.73) * mm, "end": v(0.21, 11.71) * mm});
            skLineSegment(sketch, "E46.3", {"start": v(0.21, 11.71) * mm, "end": v(0.21, 13.69) * mm});
            skLineSegment(sketch, "E46.4", {"start": v(0.21, 13.69) * mm, "end": v(1.92, 14.67) * mm});
            skLineSegment(sketch, "E46.5", {"start": v(1.92, 14.67) * mm, "end": v(3.63, 13.69) * mm});
            skPoint(sketch, "E46.0.midPoint", {"position": v(3.63, 12.7) * mm});
            skCircle(sketch, "E47.cCircle", {"center": v(7.04, 7.5) * mm, "radius": 3.41 * mm, "construction": true});
            skLineSegment(sketch, "E47.0", {"start": v(10.45, 9.48) * mm, "end": v(10.45, 5.54) * mm});
            skLineSegment(sketch, "E47.1", {"start": v(10.45, 5.54) * mm, "end": v(7.04, 3.57) * mm});
            skLineSegment(sketch, "E47.2", {"start": v(7.04, 3.57) * mm, "end": v(3.63, 5.54) * mm});
            skLineSegment(sketch, "E47.3", {"start": v(3.63, 5.54) * mm, "end": v(3.63, 9.48) * mm});
            skLineSegment(sketch, "E47.4", {"start": v(3.63, 9.48) * mm, "end": v(7.04, 11.45) * mm});
            skLineSegment(sketch, "E47.5", {"start": v(7.04, 11.45) * mm, "end": v(10.45, 9.48) * mm});
            skPoint(sketch, "E47.0.midPoint", {"position": v(10.45, 7.5) * mm});
            skCircle(sketch, "E48.cCircle", {"center": v(8.75, 18.35) * mm, "radius": 3.44 * mm, "construction": true});
            skPoint(sketch, "E48.cCircle.centerSnap0", {"position": v(8.75, 10.47) * mm});
            skLineSegment(sketch, "E48.0", {"start": v(12.18, 16.35) * mm, "end": v(8.73, 14.38) * mm});
            skLineSegment(sketch, "E48.1", {"start": v(8.73, 14.38) * mm, "end": v(5.3, 16.38) * mm});
            skLineSegment(sketch, "E48.2", {"start": v(5.3, 16.38) * mm, "end": v(5.32, 20.35) * mm});
            skLineSegment(sketch, "E48.3", {"start": v(5.32, 20.35) * mm, "end": v(8.77, 22.32) * mm});
            skLineSegment(sketch, "E48.4", {"start": v(8.77, 22.32) * mm, "end": v(12.2, 20.32) * mm});
            skLineSegment(sketch, "E48.5", {"start": v(12.2, 20.32) * mm, "end": v(12.18, 16.35) * mm});
            skPoint(sketch, "E48.0.midPoint", {"position": v(10.45, 15.36) * mm});
            skSolve(sketch);
        }
        {
            var Q0;
            Q0 = qSketchRegion(id + "F12", true);
            extrude(context, id + "F13", {"entities" : qUnion([Q0]), "operationType" : NewBodyOperationType.ADD, "depth" : 0.25 * mm});
        }
        {
            var Q0;
            Q0=makeQuery(id+"F7.opExtrude","SWEPT_FACE",FACE,{"disambiguationData":[OSD([sQuery(id+"F6.wireOp",EDGE,"E9.right")])]});
            var sketch = newSketch(context, id + "F14", { "sketchPlane" : qUnion([Q0])});
            skCircle(sketch, "E49.cCircle", {"center": v(-12.8, 21.12) * mm, "radius": 2.77 * mm, "construction": true});
            skLineSegment(sketch, "E49.0", {"start": v(-10.03, 22.72) * mm, "end": v(-10.03, 19.52) * mm});
            skLineSegment(sketch, "E49.1", {"start": v(-10.03, 19.52) * mm, "end": v(-12.8, 17.92) * mm});
            skLineSegment(sketch, "E49.2", {"start": v(-12.8, 17.92) * mm, "end": v(-15.58, 19.52) * mm});
            skLineSegment(sketch, "E49.3", {"start": v(-15.58, 19.52) * mm, "end": v(-15.58, 22.72) * mm});
            skLineSegment(sketch, "E49.4", {"start": v(-15.58, 22.72) * mm, "end": v(-12.8, 24.33) * mm});
            skLineSegment(sketch, "E49.5", {"start": v(-12.8, 24.33) * mm, "end": v(-10.03, 22.72) * mm});
            skPoint(sketch, "E49.0.midPoint", {"position": v(-10.03, 21.12) * mm});
            skCircle(sketch, "E50.cCircle", {"center": v(-11.41, 10.88) * mm, "radius": 2.91 * mm, "construction": true});
            skPoint(sketch, "E50.cCircle.centerSnap0", {"position": v(-11.41, 18.72) * mm});
            skLineSegment(sketch, "E50.0", {"start": v(-8.55, 9.12) * mm, "end": v(-11.5, 7.52) * mm});
            skLineSegment(sketch, "E50.1", {"start": v(-11.5, 7.52) * mm, "end": v(-14.37, 9.28) * mm});
            skLineSegment(sketch, "E50.2", {"start": v(-14.37, 9.28) * mm, "end": v(-14.28, 12.64) * mm});
            skLineSegment(sketch, "E50.3", {"start": v(-14.28, 12.64) * mm, "end": v(-11.32, 14.24) * mm});
            skLineSegment(sketch, "E50.4", {"start": v(-11.32, 14.24) * mm, "end": v(-8.46, 12.48) * mm});
            skLineSegment(sketch, "E50.5", {"start": v(-8.46, 12.48) * mm, "end": v(-8.55, 9.12) * mm});
            skPoint(sketch, "E50.0.midPoint", {"position": v(-10.03, 8.32) * mm});
            skCircle(sketch, "E51.cCircle", {"center": v(-5.33, 17.28) * mm, "radius": 2.77 * mm, "construction": true});
            skLineSegment(sketch, "E51.0", {"start": v(-2.56, 18.88) * mm, "end": v(-2.56, 15.68) * mm});
            skLineSegment(sketch, "E51.1", {"start": v(-2.56, 15.68) * mm, "end": v(-5.33, 14.08) * mm});
            skLineSegment(sketch, "E51.2", {"start": v(-5.33, 14.08) * mm, "end": v(-8.1, 15.68) * mm});
            skLineSegment(sketch, "E51.3", {"start": v(-8.1, 15.68) * mm, "end": v(-8.1, 18.88) * mm});
            skLineSegment(sketch, "E51.4", {"start": v(-8.1, 18.88) * mm, "end": v(-5.33, 20.48) * mm});
            skLineSegment(sketch, "E51.5", {"start": v(-5.33, 20.48) * mm, "end": v(-2.56, 18.88) * mm});
            skPoint(sketch, "E51.0.midPoint", {"position": v(-2.56, 17.28) * mm});
            skCircle(sketch, "E52.cCircle", {"center": v(-2.56, 7.52) * mm, "radius": 2.7 * mm, "construction": true});
            skLineSegment(sketch, "E52.0", {"start": v(0.14, 5.96) * mm, "end": v(-2.56, 4.4) * mm});
            skLineSegment(sketch, "E52.1", {"start": v(-2.56, 4.4) * mm, "end": v(-5.26, 5.96) * mm});
            skLineSegment(sketch, "E52.2", {"start": v(-5.26, 5.96) * mm, "end": v(-5.26, 9.08) * mm});
            skLineSegment(sketch, "E52.3", {"start": v(-5.26, 9.08) * mm, "end": v(-2.56, 10.63) * mm});
            skLineSegment(sketch, "E52.4", {"start": v(-2.56, 10.63) * mm, "end": v(0.14, 9.08) * mm});
            skLineSegment(sketch, "E52.5", {"start": v(0.14, 9.08) * mm, "end": v(0.14, 5.96) * mm});
            skPoint(sketch, "E52.0.midPoint", {"position": v(-1.21, 5.18) * mm});
            skCircle(sketch, "E53.cCircle", {"center": v(-10.67, 2.99) * mm, "radius": 1.92 * mm, "construction": true});
            skLineSegment(sketch, "E53.0", {"start": v(-8.75, 4.1) * mm, "end": v(-8.75, 1.88) * mm});
            skLineSegment(sketch, "E53.1", {"start": v(-8.75, 1.88) * mm, "end": v(-10.67, 0.77) * mm});
            skLineSegment(sketch, "E53.2", {"start": v(-10.67, 0.77) * mm, "end": v(-12.59, 1.88) * mm});
            skLineSegment(sketch, "E53.3", {"start": v(-12.59, 1.88) * mm, "end": v(-12.59, 4.1) * mm});
            skLineSegment(sketch, "E53.4", {"start": v(-12.59, 4.1) * mm, "end": v(-10.67, 5.2) * mm});
            skLineSegment(sketch, "E53.5", {"start": v(-10.67, 5.2) * mm, "end": v(-8.75, 4.1) * mm});
            skPoint(sketch, "E53.0.midPoint", {"position": v(-8.75, 2.99) * mm});
            skCircle(sketch, "E54.cCircle", {"center": v(2.35, 14.72) * mm, "radius": 2.56 * mm, "construction": true});
            skLineSegment(sketch, "E54.0", {"start": v(4.9, 16.2) * mm, "end": v(4.9, 13.24) * mm});
            skLineSegment(sketch, "E54.1", {"start": v(4.9, 13.24) * mm, "end": v(2.35, 11.77) * mm});
            skLineSegment(sketch, "E54.2", {"start": v(2.35, 11.77) * mm, "end": v(-0.21, 13.24) * mm});
            skLineSegment(sketch, "E54.3", {"start": v(-0.21, 13.24) * mm, "end": v(-0.21, 16.2) * mm});
            skLineSegment(sketch, "E54.4", {"start": v(-0.21, 16.2) * mm, "end": v(2.35, 17.68) * mm});
            skLineSegment(sketch, "E54.5", {"start": v(2.35, 17.68) * mm, "end": v(4.9, 16.2) * mm});
            skPoint(sketch, "E54.0.midPoint", {"position": v(4.9, 14.72) * mm});
            skCircle(sketch, "E55.cCircle", {"center": v(4.9, 5.18) * mm, "radius": 3.63 * mm, "construction": true});
            skLineSegment(sketch, "E55.0", {"start": v(8.53, 6.93) * mm, "end": v(8.53, 3.44) * mm});
            skLineSegment(sketch, "E55.1", {"start": v(8.53, 3.44) * mm, "end": v(5.8, 1.26) * mm});
            skLineSegment(sketch, "E55.2", {"start": v(5.8, 1.26) * mm, "end": v(2.4, 2.04) * mm});
            skLineSegment(sketch, "E55.3", {"start": v(2.4, 2.04) * mm, "end": v(0.88, 5.18) * mm});
            skLineSegment(sketch, "E55.4", {"start": v(0.88, 5.18) * mm, "end": v(2.4, 8.33) * mm});
            skLineSegment(sketch, "E55.5", {"start": v(2.4, 8.33) * mm, "end": v(5.8, 9.1) * mm});
            skLineSegment(sketch, "E55.6", {"start": v(5.8, 9.1) * mm, "end": v(8.53, 6.93) * mm});
            skPoint(sketch, "E55.0.midPoint", {"position": v(8.53, 5.18) * mm});
            skCircle(sketch, "E56.cCircle", {"center": v(0, 21.76) * mm, "radius": 2.13 * mm, "construction": true});
            skLineSegment(sketch, "E56.0", {"start": v(2.13, 23) * mm, "end": v(2.13, 20.53) * mm});
            skLineSegment(sketch, "E56.1", {"start": v(2.13, 20.53) * mm, "end": v(0, 19.3) * mm});
            skLineSegment(sketch, "E56.2", {"start": v(0, 19.3) * mm, "end": v(-2.13, 20.53) * mm});
            skLineSegment(sketch, "E56.3", {"start": v(-2.13, 20.53) * mm, "end": v(-2.13, 23) * mm});
            skLineSegment(sketch, "E56.4", {"start": v(-2.13, 23) * mm, "end": v(0, 24.23) * mm});
            skLineSegment(sketch, "E56.5", {"start": v(0, 24.23) * mm, "end": v(2.13, 23) * mm});
            skPoint(sketch, "E56.0.midPoint", {"position": v(2.13, 21.76) * mm});
            skCircle(sketch, "E57.cCircle", {"center": v(9.39, 11.73) * mm, "radius": 2.56 * mm, "construction": true});
            skLineSegment(sketch, "E57.0", {"start": v(11.95, 13.21) * mm, "end": v(11.95, 10.26) * mm});
            skLineSegment(sketch, "E57.1", {"start": v(11.95, 10.26) * mm, "end": v(9.39, 8.78) * mm});
            skLineSegment(sketch, "E57.2", {"start": v(9.39, 8.78) * mm, "end": v(6.83, 10.26) * mm});
            skLineSegment(sketch, "E57.3", {"start": v(6.83, 10.26) * mm, "end": v(6.83, 13.21) * mm});
            skLineSegment(sketch, "E57.4", {"start": v(6.83, 13.21) * mm, "end": v(9.39, 14.7) * mm});
            skLineSegment(sketch, "E57.5", {"start": v(9.39, 14.7) * mm, "end": v(11.95, 13.21) * mm});
            skPoint(sketch, "E57.0.midPoint", {"position": v(11.95, 11.73) * mm});
            skCircle(sketch, "E58.cCircle", {"center": v(13.23, 4.27) * mm, "radius": 2.35 * mm, "construction": true});
            skLineSegment(sketch, "E58.0", {"start": v(15.58, 5.62) * mm, "end": v(15.58, 2.91) * mm});
            skLineSegment(sketch, "E58.1", {"start": v(15.58, 2.91) * mm, "end": v(13.23, 1.56) * mm});
            skLineSegment(sketch, "E58.2", {"start": v(13.23, 1.56) * mm, "end": v(10.88, 2.91) * mm});
            skLineSegment(sketch, "E58.3", {"start": v(10.88, 2.91) * mm, "end": v(10.88, 5.62) * mm});
            skLineSegment(sketch, "E58.4", {"start": v(10.88, 5.62) * mm, "end": v(13.23, 6.98) * mm});
            skLineSegment(sketch, "E58.5", {"start": v(13.23, 6.98) * mm, "end": v(15.58, 5.62) * mm});
            skPoint(sketch, "E58.0.midPoint", {"position": v(15.58, 4.27) * mm});
            skCircle(sketch, "E59.cCircle", {"center": v(7.68, 21.76) * mm, "radius": 2.6 * mm, "construction": true});
            skLineSegment(sketch, "E59.0", {"start": v(10.4, 20.5) * mm, "end": v(7.94, 18.77) * mm});
            skLineSegment(sketch, "E59.1", {"start": v(7.94, 18.77) * mm, "end": v(5.22, 20.04) * mm});
            skLineSegment(sketch, "E59.2", {"start": v(5.22, 20.04) * mm, "end": v(4.96, 23.03) * mm});
            skLineSegment(sketch, "E59.3", {"start": v(4.96, 23.03) * mm, "end": v(7.42, 24.76) * mm});
            skLineSegment(sketch, "E59.4", {"start": v(7.42, 24.76) * mm, "end": v(10.14, 23.49) * mm});
            skLineSegment(sketch, "E59.5", {"start": v(10.14, 23.49) * mm, "end": v(10.4, 20.5) * mm});
            skPoint(sketch, "E59.0.midPoint", {"position": v(9.17, 19.63) * mm});
            skCircle(sketch, "E60.cCircle", {"center": v(13.23, 17.07) * mm, "radius": 2.13 * mm, "construction": true});
            skLineSegment(sketch, "E60.0", {"start": v(15.36, 18.3) * mm, "end": v(15.36, 15.84) * mm});
            skLineSegment(sketch, "E60.1", {"start": v(15.36, 15.84) * mm, "end": v(13.23, 14.6) * mm});
            skLineSegment(sketch, "E60.2", {"start": v(13.23, 14.6) * mm, "end": v(11.1, 15.84) * mm});
            skLineSegment(sketch, "E60.3", {"start": v(11.1, 15.84) * mm, "end": v(11.1, 18.3) * mm});
            skLineSegment(sketch, "E60.4", {"start": v(11.1, 18.3) * mm, "end": v(13.23, 19.53) * mm});
            skLineSegment(sketch, "E60.5", {"start": v(13.23, 19.53) * mm, "end": v(15.36, 18.3) * mm});
            skPoint(sketch, "E60.0.midPoint", {"position": v(15.36, 17.07) * mm});
            skSolve(sketch);
        }
        {
            var Q0;
            Q0 = qSketchRegion(id + "F14", true);
            extrude(context, id + "F15", {"entities" : qUnion([Q0]), "operationType" : NewBodyOperationType.ADD, "depth" : 0.25 * mm});
        }
        {
            var Q0;
            Q0=makeQuery(id+"F3.opExtrude","CAP_FACE",FACE,{"disambiguationData":[OSD([sQuery(id+"F2.wireOp",EDGE,"E2.bottom"),sQuery(id+"F2.wireOp",EDGE,"E2.top"),sQuery(id+"F2.wireOp",EDGE,"E2.left"),sQuery(id+"F2.wireOp",EDGE,"E2.right")])],"isStart":false});
            var sketch = newSketch(context, id + "F16", { "sketchPlane" : qUnion([Q0])});
            skCircle(sketch, "E61.cCircle", {"center": v(0, 0) * mm, "radius": 8.43 * mm, "construction": true});
            skLineSegment(sketch, "E61.0", {"start": v(8.43, 14.6) * mm, "end": v(8.43, -14.6) * mm});
            skLineSegment(sketch, "E61.1", {"start": v(8.43, -14.6) * mm, "end": v(-16.86, 0) * mm});
            skLineSegment(sketch, "E61.2", {"start": v(-16.86, 0) * mm, "end": v(8.43, 14.6) * mm});
            skPoint(sketch, "E61.0.midPoint", {"position": v(8.43, 0) * mm});
            skPoint(sketch, "E62.cCircle.perimeterSnap0", {"position": v(-4.21, 7.3) * mm});
            skLineSegment(sketch, "E62.0", {"start": v(-8.43, 14.6) * mm, "end": v(16.86, 0) * mm});
            skLineSegment(sketch, "E62.1", {"start": v(16.86, 0) * mm, "end": v(-8.43, -14.6) * mm});
            skLineSegment(sketch, "E62.2", {"start": v(-8.43, -14.6) * mm, "end": v(-8.43, 14.6) * mm});
            skPoint(sketch, "E62.0.midPoint", {"position": v(4.21, 7.3) * mm});
            skPoint(sketch, "E62.0.midPoint.positionSnap0", {"position": v(-4.21, 7.3) * mm});
            skCircle(sketch, "E63.cCircle", {"center": v(0, 0) * mm, "radius": 11.4 * mm, "construction": true});
            skLineSegment(sketch, "E63.0", {"start": v(12.86, -2.82) * mm, "end": v(4, -12.55) * mm});
            skLineSegment(sketch, "E63.1", {"start": v(4, -12.55) * mm, "end": v(-8.87, -9.73) * mm});
            skLineSegment(sketch, "E63.2", {"start": v(-8.87, -9.73) * mm, "end": v(-12.86, 2.82) * mm});
            skLineSegment(sketch, "E63.3", {"start": v(-12.86, 2.82) * mm, "end": v(-4, 12.55) * mm});
            skLineSegment(sketch, "E63.4", {"start": v(-4, 12.55) * mm, "end": v(8.87, 9.73) * mm});
            skLineSegment(sketch, "E63.5", {"start": v(8.87, 9.73) * mm, "end": v(12.86, -2.82) * mm});
            skPoint(sketch, "E63.0.midPoint", {"position": v(8.43, -7.68) * mm});
            skCircle(sketch, "E64", {"center": v(0, 0) * mm, "radius": 18.5 * mm});
            skSolve(sketch);
        }
        {
            var Q0;
            Q0 = qSketchRegion(id + "F16", true);
            extrude(context, id + "F17", {"entities" : qUnion([Q0]), "operationType" : NewBodyOperationType.ADD, "depth" : 0.25 * mm});
        }
        {
            var Q0;
            Q0=makeQuery(id+"F17.opExtrude","CAP_FACE",FACE,{"disambiguationData":[OSD([sQuery(id+"F16.wireOp",EDGE,"E61.0"),sQuery(id+"F16.wireOp",EDGE,"E61.1"),sQuery(id+"F16.wireOp",EDGE,"E61.2"),sQuery(id+"F16.wireOp",EDGE,"E62.0"),sQuery(id+"F16.wireOp",EDGE,"E62.1"),sQuery(id+"F16.wireOp",EDGE,"E62.2"),sQuery(id+"F16.wireOp",EDGE,"E63.0"),sQuery(id+"F16.wireOp",EDGE,"E63.1"),sQuery(id+"F16.wireOp",EDGE,"E63.2"),sQuery(id+"F16.wireOp",EDGE,"E63.3"),sQuery(id+"F16.wireOp",EDGE,"E63.4"),sQuery(id+"F16.wireOp",EDGE,"E63.5"),sQuery(id+"F16.wireOp",EDGE,"E64")])],"isStart":false});
            var sketch = newSketch(context, id + "F18", { "sketchPlane" : qUnion([Q0])});
            skCircle(sketch, "E65.cCircle", {"center": v(-13.44, 7.68) * mm, "radius": 2.07 * mm, "construction": true});
            skLineSegment(sketch, "E65.0", {"start": v(-13.16, 10.22) * mm, "end": v(-10.94, 8.2) * mm});
            skLineSegment(sketch, "E65.1", {"start": v(-10.94, 8.2) * mm, "end": v(-12.18, 5.46) * mm});
            skLineSegment(sketch, "E65.2", {"start": v(-12.18, 5.46) * mm, "end": v(-15.16, 5.8) * mm});
            skLineSegment(sketch, "E65.3", {"start": v(-15.16, 5.8) * mm, "end": v(-15.77, 8.73) * mm});
            skLineSegment(sketch, "E65.4", {"start": v(-15.77, 8.73) * mm, "end": v(-13.16, 10.22) * mm});
            skPoint(sketch, "E65.0.midPoint", {"position": v(-12.05, 9.2) * mm});
            skCircle(sketch, "E66.cCircle", {"center": v(0, 14.6) * mm, "radius": 1.91 * mm, "construction": true});
            skLineSegment(sketch, "E66.0", {"start": v(0.96, 16.75) * mm, "end": v(2.35, 14.35) * mm});
            skLineSegment(sketch, "E66.1", {"start": v(2.35, 14.35) * mm, "end": v(0.5, 12.29) * mm});
            skLineSegment(sketch, "E66.2", {"start": v(0.5, 12.29) * mm, "end": v(-2.04, 13.42) * mm});
            skLineSegment(sketch, "E66.3", {"start": v(-2.04, 13.42) * mm, "end": v(-1.75, 16.18) * mm});
            skLineSegment(sketch, "E66.4", {"start": v(-1.75, 16.18) * mm, "end": v(0.96, 16.75) * mm});
            skPoint(sketch, "E66.0.midPoint", {"position": v(1.65, 15.55) * mm});
            skCircle(sketch, "E67.cCircle", {"center": v(12.8, 7.68) * mm, "radius": 1.92 * mm, "construction": true});
            skLineSegment(sketch, "E67.0", {"start": v(14.72, 9.08) * mm, "end": v(14.72, 6.29) * mm});
            skLineSegment(sketch, "E67.1", {"start": v(14.72, 6.29) * mm, "end": v(12.07, 5.42) * mm});
            skLineSegment(sketch, "E67.2", {"start": v(12.07, 5.42) * mm, "end": v(10.43, 7.68) * mm});
            skLineSegment(sketch, "E67.3", {"start": v(10.43, 7.68) * mm, "end": v(12.07, 9.94) * mm});
            skLineSegment(sketch, "E67.4", {"start": v(12.07, 9.94) * mm, "end": v(14.72, 9.08) * mm});
            skPoint(sketch, "E67.0.midPoint", {"position": v(14.72, 7.68) * mm});
            skCircle(sketch, "E68.cCircle", {"center": v(12.86, -7.47) * mm, "radius": 2.02 * mm, "construction": true});
            skLineSegment(sketch, "E68.0", {"start": v(12.59, -9.95) * mm, "end": v(10.42, -7.97) * mm});
            skLineSegment(sketch, "E68.1", {"start": v(10.42, -7.97) * mm, "end": v(11.63, -5.3) * mm});
            skLineSegment(sketch, "E68.2", {"start": v(11.63, -5.3) * mm, "end": v(14.55, -5.62) * mm});
            skLineSegment(sketch, "E68.3", {"start": v(14.55, -5.62) * mm, "end": v(15.14, -8.5) * mm});
            skLineSegment(sketch, "E68.4", {"start": v(15.14, -8.5) * mm, "end": v(12.59, -9.95) * mm});
            skPoint(sketch, "E68.0.midPoint", {"position": v(11.5, -8.96) * mm});
            skCircle(sketch, "E69.cCircle", {"center": v(0, -14.6) * mm, "radius": 2.44 * mm, "construction": true});
            skLineSegment(sketch, "E69.0", {"start": v(2.44, -12.83) * mm, "end": v(2.44, -16.37) * mm});
            skLineSegment(sketch, "E69.1", {"start": v(2.44, -16.37) * mm, "end": v(-0.93, -17.46) * mm});
            skLineSegment(sketch, "E69.2", {"start": v(-0.93, -17.46) * mm, "end": v(-3.01, -14.6) * mm});
            skLineSegment(sketch, "E69.3", {"start": v(-3.01, -14.6) * mm, "end": v(-0.93, -11.73) * mm});
            skLineSegment(sketch, "E69.4", {"start": v(-0.93, -11.73) * mm, "end": v(2.44, -12.83) * mm});
            skPoint(sketch, "E69.0.midPoint", {"position": v(2.44, -14.6) * mm});
            skCircle(sketch, "E70.cCircle", {"center": v(-12.86, -7.68) * mm, "radius": 2.31 * mm, "construction": true});
            skLineSegment(sketch, "E70.0", {"start": v(-10, -7.56) * mm, "end": v(-11.87, -10.36) * mm});
            skLineSegment(sketch, "E70.1", {"start": v(-11.87, -10.36) * mm, "end": v(-15.1, -9.45) * mm});
            skLineSegment(sketch, "E70.2", {"start": v(-15.1, -9.45) * mm, "end": v(-15.24, -6.1) * mm});
            skLineSegment(sketch, "E70.3", {"start": v(-15.24, -6.1) * mm, "end": v(-12.1, -4.93) * mm});
            skLineSegment(sketch, "E70.4", {"start": v(-12.1, -4.93) * mm, "end": v(-10, -7.56) * mm});
            skPoint(sketch, "E70.0.midPoint", {"position": v(-10.94, -8.96) * mm});
            skSolve(sketch);
        }
        {
            var Q0;
            Q0 = qSketchRegion(id + "F18", true);
            extrude(context, id + "F19", {"entities" : qUnion([Q0]), "operationType" : NewBodyOperationType.ADD, "depth" : 0.25 * mm});
        }
        {
            var Q0;
            Q0=makeQuery(id+"F7.boolean.opBoolean","MERGE",FACE,{"derivedFrom":[makeQuery(id+"F5.boolean.opBoolean","MERGE",FACE,{"derivedFrom":[makeQuery(id+"F1.opExtrude","CAP_FACE",FACE,{"disambiguationData":[OSD([sQuery(id+"F0.wireOp",EDGE,"E0.bottom"),sQuery(id+"F0.wireOp",EDGE,"E0.top"),sQuery(id+"F0.wireOp",EDGE,"E0.left"),sQuery(id+"F0.wireOp",EDGE,"E0.right"),sQuery(id+"F0.wireOp",EDGE,"E1.bottom"),sQuery(id+"F0.wireOp",EDGE,"E1.top"),sQuery(id+"F0.wireOp",EDGE,"E1.left"),sQuery(id+"F0.wireOp",EDGE,"E1.right")])],"isStart":false}),makeQuery(id+"F5.opExtrude","CAP_FACE",FACE,{"disambiguationData":[OSD([sQuery(id+"F4.wireOp",EDGE,"E3")])],"isStart":false}),makeQuery(id+"F5.opExtrude","CAP_FACE",FACE,{"disambiguationData":[OSD([sQuery(id+"F4.wireOp",EDGE,"E4")])],"isStart":false}),makeQuery(id+"F5.opExtrude","CAP_FACE",FACE,{"disambiguationData":[OSD([sQuery(id+"F4.wireOp",EDGE,"E5")])],"isStart":false}),makeQuery(id+"F5.opExtrude","CAP_FACE",FACE,{"disambiguationData":[OSD([sQuery(id+"F4.wireOp",EDGE,"E6")])],"isStart":false})]}),makeQuery(id+"F7.opExtrude","CAP_FACE",FACE,{"disambiguationData":[OSD([sQuery(id+"F6.wireOp",EDGE,"E7.bottom"),sQuery(id+"F6.wireOp",EDGE,"E7.top"),sQuery(id+"F6.wireOp",EDGE,"E7.left"),sQuery(id+"F6.wireOp",EDGE,"E7.right")])],"isStart":false}),makeQuery(id+"F7.opExtrude","CAP_FACE",FACE,{"disambiguationData":[OSD([sQuery(id+"F6.wireOp",EDGE,"E8.bottom"),sQuery(id+"F6.wireOp",EDGE,"E8.top"),sQuery(id+"F6.wireOp",EDGE,"E8.left"),sQuery(id+"F6.wireOp",EDGE,"E8.right")])],"isStart":false}),makeQuery(id+"F7.opExtrude","CAP_FACE",FACE,{"disambiguationData":[OSD([sQuery(id+"F6.wireOp",EDGE,"E9.bottom"),sQuery(id+"F6.wireOp",EDGE,"E9.top"),sQuery(id+"F6.wireOp",EDGE,"E9.left"),sQuery(id+"F6.wireOp",EDGE,"E9.right")])],"isStart":false}),makeQuery(id+"F7.opExtrude","CAP_FACE",FACE,{"disambiguationData":[OSD([sQuery(id+"F6.wireOp",EDGE,"E10.bottom"),sQuery(id+"F6.wireOp",EDGE,"E10.top"),sQuery(id+"F6.wireOp",EDGE,"E10.left"),sQuery(id+"F6.wireOp",EDGE,"E10.right")])],"isStart":false})]});
            var sketch = newSketch(context, id + "F20", { "sketchPlane" : qUnion([Q0])});
            skLineSegment(sketch, "E71.bottom", {"start": v(27.1, 20.7) * mm, "end": v(-27.1, 20.7) * mm});
            skLineSegment(sketch, "E71.top", {"start": v(27.1, 20.27) * mm, "end": v(-27.1, 20.27) * mm});
            skLineSegment(sketch, "E71.left", {"start": v(27.1, 20.7) * mm, "end": v(27.1, 20.27) * mm});
            skLineSegment(sketch, "E71.right", {"start": v(-27.1, 20.7) * mm, "end": v(-27.1, 20.27) * mm});
            skPoint(sketch, "E71.middle", {"position": v(0, 20.48) * mm});
            skPoint(sketch, "E71.middle.positionSnap0", {"position": v(0, 18.56) * mm});
            skPoint(sketch, "E71.centerSnap0", {"position": v(0, 18.56) * mm});
            skLineSegment(sketch, "E72.bottom", {"start": v(26.52, -20.7) * mm, "end": v(-26.52, -20.7) * mm});
            skLineSegment(sketch, "E72.top", {"start": v(26.52, -21.01) * mm, "end": v(-26.52, -21.01) * mm});
            skLineSegment(sketch, "E72.left", {"start": v(26.52, -20.7) * mm, "end": v(26.52, -21.01) * mm});
            skLineSegment(sketch, "E72.right", {"start": v(-26.52, -20.7) * mm, "end": v(-26.52, -21.01) * mm});
            skPoint(sketch, "E72.middle", {"position": v(0, -20.85) * mm});
            skSolve(sketch);
        }
        {
            var Q0;
            Q0 = qSketchRegion(id + "F20", true);
            extrude(context, id + "F21", {"entities" : qUnion([Q0]), "operationType" : NewBodyOperationType.ADD, "depth" : 0.25 * mm});
        }
        {
            var Q0;
            Q0=makeQuery(id+"F1.opExtrude","SWEPT_FACE",FACE,{"disambiguationData":[OSD([sQuery(id+"F0.wireOp",EDGE,"E1.top")])]});
            var sketch = newSketch(context, id + "F22", { "sketchPlane" : qUnion([Q0])});
            skCircle(sketch, "E73.cCircle", {"center": v(0, 16.2) * mm, "radius": 6.5 * mm, "construction": true});
            skLineSegment(sketch, "E73.0", {"start": v(-6.5, 12.45) * mm, "end": v(-6.5, 19.96) * mm});
            skLineSegment(sketch, "E73.1", {"start": v(-6.5, 19.96) * mm, "end": v(0, 23.72) * mm});
            skLineSegment(sketch, "E73.2", {"start": v(0, 23.72) * mm, "end": v(6.5, 19.96) * mm});
            skLineSegment(sketch, "E73.3", {"start": v(6.5, 19.96) * mm, "end": v(6.5, 12.45) * mm});
            skLineSegment(sketch, "E73.4", {"start": v(6.5, 12.45) * mm, "end": v(0, 8.7) * mm});
            skLineSegment(sketch, "E73.5", {"start": v(0, 8.7) * mm, "end": v(-6.5, 12.45) * mm});
            skPoint(sketch, "E73.0.midPoint", {"position": v(-6.5, 16.2) * mm});
            skCircle(sketch, "E74.cCircle", {"center": v(0, 16.2) * mm, "radius": 3.68 * mm, "construction": true});
            skLineSegment(sketch, "E74.0", {"start": v(1.99, 19.95) * mm, "end": v(4.24, 16.36) * mm});
            skLineSegment(sketch, "E74.1", {"start": v(4.24, 16.36) * mm, "end": v(2.25, 12.6) * mm});
            skLineSegment(sketch, "E74.2", {"start": v(2.25, 12.6) * mm, "end": v(-1.99, 12.45) * mm});
            skLineSegment(sketch, "E74.3", {"start": v(-1.99, 12.45) * mm, "end": v(-4.24, 16.05) * mm});
            skLineSegment(sketch, "E74.4", {"start": v(-4.24, 16.05) * mm, "end": v(-2.25, 19.8) * mm});
            skLineSegment(sketch, "E74.5", {"start": v(-2.25, 19.8) * mm, "end": v(1.99, 19.95) * mm});
            skPoint(sketch, "E74.0.midPoint", {"position": v(3.11, 18.15) * mm});
            skCircle(sketch, "E75.cCircle", {"center": v(-20.26, 15.13) * mm, "radius": 3.44 * mm, "construction": true});
            skLineSegment(sketch, "E75.0", {"start": v(-16.82, 21.08) * mm, "end": v(-16.82, 9.17) * mm});
            skLineSegment(sketch, "E75.1", {"start": v(-16.82, 9.17) * mm, "end": v(-27.14, 15.13) * mm});
            skLineSegment(sketch, "E75.2", {"start": v(-27.14, 15.13) * mm, "end": v(-16.82, 21.08) * mm});
            skPoint(sketch, "E75.0.midPoint", {"position": v(-16.82, 15.13) * mm});
            skCircle(sketch, "E76.cCircle", {"center": v(17.83, 15.13) * mm, "radius": 3.26 * mm, "construction": true});
            skLineSegment(sketch, "E76.0", {"start": v(15.53, 21.22) * mm, "end": v(24.26, 14.07) * mm});
            skLineSegment(sketch, "E76.1", {"start": v(24.26, 14.07) * mm, "end": v(13.7, 10.09) * mm});
            skLineSegment(sketch, "E76.2", {"start": v(13.7, 10.09) * mm, "end": v(15.53, 21.22) * mm});
            skPoint(sketch, "E76.0.midPoint", {"position": v(19.9, 17.65) * mm});
            skSolve(sketch);
        }
        {
            var Q0;
            Q0 = qSketchRegion(id + "F22", true);
            extrude(context, id + "F23", {"entities" : qUnion([Q0]), "operationType" : NewBodyOperationType.ADD, "depth" : 0.25 * mm});
        }
        {
            var Q0;
            Q0=makeQuery(id+"F1.opExtrude","SWEPT_FACE",FACE,{"disambiguationData":[OSD([sQuery(id+"F0.wireOp",EDGE,"E1.bottom")])]});
            var sketch = newSketch(context, id + "F24", { "sketchPlane" : qUnion([Q0])});
            skCircle(sketch, "E77.cCircle", {"center": v(0, 16.16) * mm, "radius": 5.82 * mm, "construction": true});
            skLineSegment(sketch, "E77.0", {"start": v(5.82, 19.52) * mm, "end": v(5.82, 12.8) * mm});
            skLineSegment(sketch, "E77.1", {"start": v(5.82, 12.8) * mm, "end": v(0, 9.44) * mm});
            skLineSegment(sketch, "E77.2", {"start": v(0, 9.44) * mm, "end": v(-5.82, 12.8) * mm});
            skLineSegment(sketch, "E77.3", {"start": v(-5.82, 12.8) * mm, "end": v(-5.82, 19.52) * mm});
            skLineSegment(sketch, "E77.4", {"start": v(-5.82, 19.52) * mm, "end": v(0, 22.87) * mm});
            skLineSegment(sketch, "E77.5", {"start": v(0, 22.87) * mm, "end": v(5.82, 19.52) * mm});
            skPoint(sketch, "E77.0.midPoint", {"position": v(5.82, 16.16) * mm});
            skCircle(sketch, "E78.cCircle", {"center": v(0, 16.16) * mm, "radius": 2.99 * mm, "construction": true});
            skLineSegment(sketch, "E78.0", {"start": v(2.99, 17.88) * mm, "end": v(2.99, 14.43) * mm});
            skLineSegment(sketch, "E78.1", {"start": v(2.99, 14.43) * mm, "end": v(0, 12.7) * mm});
            skLineSegment(sketch, "E78.2", {"start": v(0, 12.7) * mm, "end": v(-2.99, 14.43) * mm});
            skLineSegment(sketch, "E78.3", {"start": v(-2.99, 14.43) * mm, "end": v(-2.99, 17.88) * mm});
            skLineSegment(sketch, "E78.4", {"start": v(-2.99, 17.88) * mm, "end": v(0, 19.6) * mm});
            skLineSegment(sketch, "E78.5", {"start": v(0, 19.6) * mm, "end": v(2.99, 17.88) * mm});
            skPoint(sketch, "E78.0.midPoint", {"position": v(2.99, 16.16) * mm});
            skCircle(sketch, "E79.cCircle", {"center": v(-20.27, 16.16) * mm, "radius": 3.65 * mm, "construction": true});
            skLineSegment(sketch, "E79.0", {"start": v(-20.05, 23.45) * mm, "end": v(-14.07, 12.32) * mm});
            skLineSegment(sketch, "E79.1", {"start": v(-14.07, 12.32) * mm, "end": v(-26.7, 12.7) * mm});
            skLineSegment(sketch, "E79.2", {"start": v(-26.7, 12.7) * mm, "end": v(-20.05, 23.45) * mm});
            skPoint(sketch, "E79.0.midPoint", {"position": v(-17.06, 17.88) * mm});
            skCircle(sketch, "E80.cCircle", {"center": v(18.78, 16.16) * mm, "radius": 3.49 * mm, "construction": true});
            skLineSegment(sketch, "E80.0", {"start": v(18.82, 23.13) * mm, "end": v(24.8, 12.63) * mm});
            skLineSegment(sketch, "E80.1", {"start": v(24.8, 12.63) * mm, "end": v(12.71, 12.7) * mm});
            skLineSegment(sketch, "E80.2", {"start": v(12.71, 12.7) * mm, "end": v(18.82, 23.13) * mm});
            skPoint(sketch, "E80.0.midPoint", {"position": v(21.81, 17.88) * mm});
            skSolve(sketch);
        }
        {
            var Q0;
            Q0 = qSketchRegion(id + "F24", true);
            extrude(context, id + "F25", {"entities" : qUnion([Q0]), "operationType" : NewBodyOperationType.ADD, "depth" : 0.25 * mm});
        }
        {
            var Q0;
            Q0=makeQuery(id+"F1.opExtrude","SWEPT_FACE",FACE,{"disambiguationData":[OSD([sQuery(id+"F0.wireOp",EDGE,"E1.right")])]});
            var sketch = newSketch(context, id + "F26", { "sketchPlane" : qUnion([Q0])});
            skCircle(sketch, "E81.cCircle", {"center": v(0, 14.6) * mm, "radius": 5.99 * mm, "construction": true});
            skLineSegment(sketch, "E81.0", {"start": v(5.99, 18.05) * mm, "end": v(5.99, 11.14) * mm});
            skLineSegment(sketch, "E81.1", {"start": v(5.99, 11.14) * mm, "end": v(0, 7.69) * mm});
            skLineSegment(sketch, "E81.2", {"start": v(0, 7.69) * mm, "end": v(-5.99, 11.14) * mm});
            skLineSegment(sketch, "E81.3", {"start": v(-5.99, 11.14) * mm, "end": v(-5.99, 18.05) * mm});
            skLineSegment(sketch, "E81.4", {"start": v(-5.99, 18.05) * mm, "end": v(0, 21.51) * mm});
            skLineSegment(sketch, "E81.5", {"start": v(0, 21.51) * mm, "end": v(5.99, 18.05) * mm});
            skPoint(sketch, "E81.0.midPoint", {"position": v(5.99, 14.6) * mm});
            skCircle(sketch, "E82.cCircle", {"center": v(0, 14.6) * mm, "radius": 3.21 * mm, "construction": true});
            skLineSegment(sketch, "E82.0", {"start": v(3.21, 16.45) * mm, "end": v(3.21, 12.74) * mm});
            skLineSegment(sketch, "E82.1", {"start": v(3.21, 12.74) * mm, "end": v(0, 10.89) * mm});
            skLineSegment(sketch, "E82.2", {"start": v(0, 10.89) * mm, "end": v(-3.21, 12.74) * mm});
            skLineSegment(sketch, "E82.3", {"start": v(-3.21, 12.74) * mm, "end": v(-3.21, 16.45) * mm});
            skLineSegment(sketch, "E82.4", {"start": v(-3.21, 16.45) * mm, "end": v(0, 18.3) * mm});
            skLineSegment(sketch, "E82.5", {"start": v(0, 18.3) * mm, "end": v(3.21, 16.45) * mm});
            skPoint(sketch, "E82.0.midPoint", {"position": v(3.21, 14.6) * mm});
            skSolve(sketch);
        }
        {
            var Q0;
            Q0 = qSketchRegion(id + "F26", true);
            extrude(context, id + "F27", {"entities" : qUnion([Q0]), "operationType" : NewBodyOperationType.ADD, "depth" : 0.25 * mm});
        }
        {
            var Q0;
            Q0=makeQuery(id+"F1.opExtrude","SWEPT_FACE",FACE,{"disambiguationData":[OSD([sQuery(id+"F0.wireOp",EDGE,"E1.left")])]});
            var sketch = newSketch(context, id + "F28", { "sketchPlane" : qUnion([Q0])});
            skCircle(sketch, "E83.cCircle", {"center": v(0, 14.02) * mm, "radius": 5.68 * mm, "construction": true});
            skLineSegment(sketch, "E83.0", {"start": v(5.68, 17.3) * mm, "end": v(5.68, 10.74) * mm});
            skLineSegment(sketch, "E83.1", {"start": v(5.68, 10.74) * mm, "end": v(0, 7.46) * mm});
            skLineSegment(sketch, "E83.2", {"start": v(0, 7.46) * mm, "end": v(-5.68, 10.74) * mm});
            skLineSegment(sketch, "E83.3", {"start": v(-5.68, 10.74) * mm, "end": v(-5.68, 17.3) * mm});
            skLineSegment(sketch, "E83.4", {"start": v(-5.68, 17.3) * mm, "end": v(0, 20.58) * mm});
            skLineSegment(sketch, "E83.5", {"start": v(0, 20.58) * mm, "end": v(5.68, 17.3) * mm});
            skPoint(sketch, "E83.0.midPoint", {"position": v(5.68, 14.02) * mm});
            skCircle(sketch, "E84.cCircle", {"center": v(0, 14.02) * mm, "radius": 2.84 * mm, "construction": true});
            skPoint(sketch, "E84.cCircle.perimeterSnap0", {"position": v(2.84, 9.1) * mm});
            skLineSegment(sketch, "E84.0", {"start": v(2.84, 15.66) * mm, "end": v(2.84, 12.38) * mm});
            skLineSegment(sketch, "E84.1", {"start": v(2.84, 12.38) * mm, "end": v(0, 10.74) * mm});
            skLineSegment(sketch, "E84.2", {"start": v(0, 10.74) * mm, "end": v(-2.84, 12.38) * mm});
            skLineSegment(sketch, "E84.3", {"start": v(-2.84, 12.38) * mm, "end": v(-2.84, 15.66) * mm});
            skLineSegment(sketch, "E84.4", {"start": v(-2.84, 15.66) * mm, "end": v(0, 17.3) * mm});
            skLineSegment(sketch, "E84.5", {"start": v(0, 17.3) * mm, "end": v(2.84, 15.66) * mm});
            skPoint(sketch, "E84.0.midPoint", {"position": v(2.84, 14.02) * mm});
            skPoint(sketch, "E84.0.midPoint.positionSnap0", {"position": v(2.84, 9.1) * mm});
            skSolve(sketch);
        }
        {
            var Q0;
            Q0 = qSketchRegion(id + "F28", true);
            extrude(context, id + "F29", {"entities" : qUnion([Q0]), "operationType" : NewBodyOperationType.ADD, "depth" : 0.25 * mm});
        }
        {
            var Q0;
            {var subQ12=sQuery(id+"F0.wireOp",EDGE,"E1.bottom");var subQ22=sQuery(id+"F0.wireOp",EDGE,"E1.left");Q0=makeQuery(id+"F29.boolean.opBoolean","SPLIT",FACE,{"disambiguationData":[TD([makeQuery(id+"F1.opExtrude","SWEPT_FACE",FACE,{"disambiguationData":[OSD([subQ12])]})])],"derivedFrom":makeQuery(id+"F1.opExtrude","SWEPT_FACE",FACE,{"disambiguationData":[OSD([subQ22])]})});}
            var sketch = newSketch(context, id + "F30", { "sketchPlane" : qUnion([Q0])});
            skCircle(sketch, "E85.cCircle", {"center": v(-12.36, 12.7) * mm, "radius": 2.77 * mm, "construction": true});
            skPoint(sketch, "E85.cCircle.centerSnap0", {"position": v(-18.56, 12.7) * mm});
            skLineSegment(sketch, "E85.0", {"start": v(-9.6, 17.5) * mm, "end": v(-9.6, 7.9) * mm});
            skLineSegment(sketch, "E85.1", {"start": v(-9.6, 7.9) * mm, "end": v(-17.91, 12.7) * mm});
            skLineSegment(sketch, "E85.2", {"start": v(-17.91, 12.7) * mm, "end": v(-9.6, 17.5) * mm});
            skPoint(sketch, "E85.0.midPoint", {"position": v(-9.6, 12.7) * mm});
            skCircle(sketch, "E86.cCircle", {"center": v(13.02, 14.02) * mm, "radius": 2.35 * mm, "construction": true});
            skPoint(sketch, "E86.cCircle.centerSnap0", {"position": v(5.68, 14.02) * mm});
            skLineSegment(sketch, "E86.0", {"start": v(15.38, 18.1) * mm, "end": v(15.38, 9.94) * mm});
            skLineSegment(sketch, "E86.1", {"start": v(15.38, 9.94) * mm, "end": v(8.32, 14.02) * mm});
            skLineSegment(sketch, "E86.2", {"start": v(8.32, 14.02) * mm, "end": v(15.38, 18.1) * mm});
            skPoint(sketch, "E86.0.midPoint", {"position": v(15.38, 14.02) * mm});
            skSolve(sketch);
        }
        {
            var Q0;
            Q0 = qSketchRegion(id + "F30", true);
            extrude(context, id + "F31", {"entities" : qUnion([Q0]), "operationType" : NewBodyOperationType.ADD, "depth" : 0.25 * mm});
        }
        {
            var Q0;
            {var subQ12=sQuery(id+"F0.wireOp",EDGE,"E1.bottom");var subQ21=sQuery(id+"F0.wireOp",EDGE,"E1.right");Q0=makeQuery(id+"F27.boolean.opBoolean","SPLIT",FACE,{"disambiguationData":[TD([makeQuery(id+"F1.opExtrude","SWEPT_FACE",FACE,{"disambiguationData":[OSD([subQ12])]})])],"derivedFrom":makeQuery(id+"F1.opExtrude","SWEPT_FACE",FACE,{"disambiguationData":[OSD([subQ21])]})});}
            var sketch = newSketch(context, id + "F32", { "sketchPlane" : qUnion([Q0])});
            skCircle(sketch, "E87.cCircle", {"center": v(-12.68, 14.3) * mm, "radius": 2.77 * mm, "construction": true});
            skLineSegment(sketch, "E87.0", {"start": v(-9.9, 19.1) * mm, "end": v(-9.9, 9.5) * mm});
            skLineSegment(sketch, "E87.1", {"start": v(-9.9, 9.5) * mm, "end": v(-18.23, 14.3) * mm});
            skLineSegment(sketch, "E87.2", {"start": v(-18.23, 14.3) * mm, "end": v(-9.9, 19.1) * mm});
            skPoint(sketch, "E87.0.midPoint", {"position": v(-9.9, 14.3) * mm});
            skCircle(sketch, "E88.cCircle", {"center": v(12.4, 12.7) * mm, "radius": 2.18 * mm, "construction": true});
            skPoint(sketch, "E88.cCircle.centerSnap0", {"position": v(18.56, 12.7) * mm});
            skLineSegment(sketch, "E88.0", {"start": v(14.58, 16.47) * mm, "end": v(14.58, 8.93) * mm});
            skLineSegment(sketch, "E88.1", {"start": v(14.58, 8.93) * mm, "end": v(8.05, 12.7) * mm});
            skLineSegment(sketch, "E88.2", {"start": v(8.05, 12.7) * mm, "end": v(14.58, 16.47) * mm});
            skPoint(sketch, "E88.0.midPoint", {"position": v(14.58, 12.7) * mm});
            skSolve(sketch);
        }
        {
            var Q0;
            Q0 = qSketchRegion(id + "F32", true);
            extrude(context, id + "F33", {"entities" : qUnion([Q0]), "operationType" : NewBodyOperationType.ADD, "depth" : 0.25 * mm});
        }
        {
            var Q0;
            {var subQ17=sQuery(id+"F16.wireOp",EDGE,"E61.0");var subQ22=sQuery(id+"F16.wireOp",EDGE,"E61.2");var subQ30=makeQuery(id+"F16.imprint","INTERSECT",VERTEX,{"derivedFrom":[subQ17,subQ22]});Q0=makeQuery(id+"F17.boolean.opBoolean","SPLIT",FACE,{"disambiguationData":[TD([makeQuery(id+"F17.opExtrude","SWEPT_FACE",FACE,{"disambiguationData":[OSD([subQ17]),TDD([makeQuery(id+"F16.imprint","IMPRINT",EDGE,{"disambiguationData":[TD([[subQ30,-1.0]])],"derivedFrom":subQ17})])]})])],"derivedFrom":makeQuery(id+"F3.opExtrude","CAP_FACE",FACE,{"disambiguationData":[OSD([sQuery(id+"F2.wireOp",EDGE,"E2.bottom"),sQuery(id+"F2.wireOp",EDGE,"E2.top"),sQuery(id+"F2.wireOp",EDGE,"E2.left"),sQuery(id+"F2.wireOp",EDGE,"E2.right")])],"isStart":false})});}
            var sketch = newSketch(context, id + "F34", { "sketchPlane" : qUnion([Q0])});
            skCircle(sketch, "E89.cCircle", {"center": v(0, 0) * mm, "radius": 4.67 * mm, "construction": true});
            skLineSegment(sketch, "E89.0", {"start": v(8.09, 4.67) * mm, "end": v(0, -9.34) * mm});
            skLineSegment(sketch, "E89.1", {"start": v(0, -9.34) * mm, "end": v(-8.09, 4.67) * mm});
            skLineSegment(sketch, "E89.2", {"start": v(-8.09, 4.67) * mm, "end": v(8.09, 4.67) * mm});
            skPoint(sketch, "E89.0.midPoint", {"position": v(4.04, -2.33) * mm});
            skLineSegment(sketch, "E90.0", {"start": v(0, 9.34) * mm, "end": v(8.09, -4.67) * mm});
            skLineSegment(sketch, "E90.1", {"start": v(8.09, -4.67) * mm, "end": v(-8.09, -4.67) * mm});
            skLineSegment(sketch, "E90.2", {"start": v(-8.09, -4.67) * mm, "end": v(0, 9.34) * mm});
            skPoint(sketch, "E90.0.midPoint", {"position": v(4.04, 2.33) * mm});
            skCircle(sketch, "E91.cCircle", {"center": v(0, 0) * mm, "radius": 7.38 * mm, "construction": true});
            skLineSegment(sketch, "E91.0", {"start": v(5, 7.63) * mm, "end": v(8.8, -2.4) * mm});
            skLineSegment(sketch, "E91.1", {"start": v(8.8, -2.4) * mm, "end": v(0.44, -9.1) * mm});
            skLineSegment(sketch, "E91.2", {"start": v(0.44, -9.1) * mm, "end": v(-8.53, -3.23) * mm});
            skLineSegment(sketch, "E91.3", {"start": v(-8.53, -3.23) * mm, "end": v(-5.7, 7.11) * mm});
            skLineSegment(sketch, "E91.4", {"start": v(-5.7, 7.11) * mm, "end": v(5, 7.63) * mm});
            skPoint(sketch, "E91.0.midPoint", {"position": v(6.9, 2.61) * mm});
            skSolve(sketch);
        }
        {
            var Q0;
            Q0 = qSketchRegion(id + "F34", true);
            extrude(context, id + "F35", {"entities" : qUnion([Q0]), "operationType" : NewBodyOperationType.ADD, "depth" : 0.25 * mm});
        }
        {
            var Q0;
            Q0=makeQuery(id+"F7.boolean.opBoolean","MERGE",FACE,{"derivedFrom":[makeQuery(id+"F5.boolean.opBoolean","MERGE",FACE,{"derivedFrom":[makeQuery(id+"F3.boolean.opBoolean","MERGE",FACE,{"derivedFrom":[makeQuery(id+"F1.opExtrude","CAP_FACE",FACE,{"disambiguationData":[OSD([sQuery(id+"F0.wireOp",EDGE,"E0.bottom"),sQuery(id+"F0.wireOp",EDGE,"E0.top"),sQuery(id+"F0.wireOp",EDGE,"E0.left"),sQuery(id+"F0.wireOp",EDGE,"E0.right"),sQuery(id+"F0.wireOp",EDGE,"E1.bottom"),sQuery(id+"F0.wireOp",EDGE,"E1.top"),sQuery(id+"F0.wireOp",EDGE,"E1.left"),sQuery(id+"F0.wireOp",EDGE,"E1.right")])],"isStart":true}),makeQuery(id+"F3.opExtrude","CAP_FACE",FACE,{"disambiguationData":[OSD([sQuery(id+"F2.wireOp",EDGE,"E2.bottom"),sQuery(id+"F2.wireOp",EDGE,"E2.top"),sQuery(id+"F2.wireOp",EDGE,"E2.left"),sQuery(id+"F2.wireOp",EDGE,"E2.right")])],"isStart":true})]}),makeQuery(id+"F5.opExtrude","CAP_FACE",FACE,{"disambiguationData":[OSD([sQuery(id+"F4.wireOp",EDGE,"E3")])],"isStart":true}),makeQuery(id+"F5.opExtrude","CAP_FACE",FACE,{"disambiguationData":[OSD([sQuery(id+"F4.wireOp",EDGE,"E4")])],"isStart":true}),makeQuery(id+"F5.opExtrude","CAP_FACE",FACE,{"disambiguationData":[OSD([sQuery(id+"F4.wireOp",EDGE,"E5")])],"isStart":true}),makeQuery(id+"F5.opExtrude","CAP_FACE",FACE,{"disambiguationData":[OSD([sQuery(id+"F4.wireOp",EDGE,"E6")])],"isStart":true})]}),makeQuery(id+"F7.opExtrude","CAP_FACE",FACE,{"disambiguationData":[OSD([sQuery(id+"F6.wireOp",EDGE,"E7.bottom"),sQuery(id+"F6.wireOp",EDGE,"E7.top"),sQuery(id+"F6.wireOp",EDGE,"E7.left"),sQuery(id+"F6.wireOp",EDGE,"E7.right")])],"isStart":true}),makeQuery(id+"F7.opExtrude","CAP_FACE",FACE,{"disambiguationData":[OSD([sQuery(id+"F6.wireOp",EDGE,"E8.bottom"),sQuery(id+"F6.wireOp",EDGE,"E8.top"),sQuery(id+"F6.wireOp",EDGE,"E8.left"),sQuery(id+"F6.wireOp",EDGE,"E8.right")])],"isStart":true}),makeQuery(id+"F7.opExtrude","CAP_FACE",FACE,{"disambiguationData":[OSD([sQuery(id+"F6.wireOp",EDGE,"E9.bottom"),sQuery(id+"F6.wireOp",EDGE,"E9.top"),sQuery(id+"F6.wireOp",EDGE,"E9.left"),sQuery(id+"F6.wireOp",EDGE,"E9.right")])],"isStart":true}),makeQuery(id+"F7.opExtrude","CAP_FACE",FACE,{"disambiguationData":[OSD([sQuery(id+"F6.wireOp",EDGE,"E10.bottom"),sQuery(id+"F6.wireOp",EDGE,"E10.top"),sQuery(id+"F6.wireOp",EDGE,"E10.left"),sQuery(id+"F6.wireOp",EDGE,"E10.right")])],"isStart":true})]});
            var sketch = newSketch(context, id + "F36", { "sketchPlane" : qUnion([Q0])});
            skCircle(sketch, "E92.cCircle", {"center": v(-23.25, 16.75) * mm, "radius": 2.96 * mm, "construction": true});
            skPoint(sketch, "E92.0.midPoint", {"position": v(-20.3, 16.75) * mm});
            skCircle(sketch, "E93.cCircle", {"center": v(-23.25, 16.75) * mm, "radius": 3.41 * mm, "construction": true});
            skLineSegment(sketch, "E93.0", {"start": v(-17.34, 20.16) * mm, "end": v(-23.25, 9.92) * mm});
            skLineSegment(sketch, "E93.1", {"start": v(-23.25, 9.92) * mm, "end": v(-29.17, 20.16) * mm});
            skLineSegment(sketch, "E93.2", {"start": v(-29.17, 20.16) * mm, "end": v(-17.34, 20.16) * mm});
            skPoint(sketch, "E93.0.midPoint", {"position": v(-20.3, 15.04) * mm});
            skCircle(sketch, "E94", {"center": v(22.86, 15.04) * mm, "radius": 5 * mm});
            skPoint(sketch, "E94.centerSnap0", {"position": v(-26.21, 15.04) * mm});
            skLineSegment(sketch, "E95.bottom", {"start": v(-19.31, -20.7) * mm, "end": v(-27.2, -20.7) * mm});
            skLineSegment(sketch, "E95.top", {"start": v(-19.31, -14.3) * mm, "end": v(-27.2, -14.3) * mm});
            skLineSegment(sketch, "E95.left", {"start": v(-19.31, -20.7) * mm, "end": v(-19.31, -14.3) * mm});
            skLineSegment(sketch, "E95.right", {"start": v(-27.2, -20.7) * mm, "end": v(-27.2, -14.3) * mm});
            skPoint(sketch, "E95.middle", {"position": v(-23.25, -17.5) * mm});
            skLineSegment(sketch, "E96.bottom", {"start": v(22.7, -14.11) * mm, "end": v(24.88, -14.11) * mm});
            skLineSegment(sketch, "E96.top", {"start": v(22.7, -20.88) * mm, "end": v(24.88, -20.88) * mm});
            skLineSegment(sketch, "E97.left", {"start": v(23.65, -18.56) * mm, "end": v(23.65, -16.43) * mm});
            skLineSegment(sketch, "E97.right", {"start": v(20, -18.56) * mm, "end": v(20, -16.43) * mm});
            skLineSegment(sketch, "E98.top", {"start": v(23.65, -14.3) * mm, "end": v(23.65, -14.3) * mm});
            skLineSegment(sketch, "E98.left", {"start": v(23.65, -18.56) * mm, "end": v(23.65, -14.3) * mm});
            skLineSegment(sketch, "E98.right", {"start": v(23.65, -18.56) * mm, "end": v(23.65, -14.3) * mm});
            skPoint(sketch, "E98.middle", {"position": v(23.65, -16.43) * mm});
            skLineSegment(sketch, "E99.bottom", {"start": v(24.88, -20.88) * mm, "end": v(22.42, -20.88) * mm});
            skLineSegment(sketch, "E99.top", {"start": v(24.88, -11.98) * mm, "end": v(22.42, -11.98) * mm});
            skLineSegment(sketch, "E99.left", {"start": v(24.88, -20.88) * mm, "end": v(24.88, -11.98) * mm});
            skLineSegment(sketch, "E99.right", {"start": v(22.42, -20.88) * mm, "end": v(22.42, -11.98) * mm});
            skLineSegment(sketch, "E100.bottom", {"start": v(23.65, -18.56) * mm, "end": v(23.65, -18.56) * mm});
            skLineSegment(sketch, "E101.left", {"start": v(24.88, -11.98) * mm, "end": v(24.88, -20.88) * mm});
            skLineSegment(sketch, "E101.right", {"start": v(22.42, -11.98) * mm, "end": v(22.42, -20.88) * mm});
            skSolve(sketch);
        }
        {
            var Q0;
            Q0 = qSketchRegion(id + "F36", true);
            extrude(context, id + "F37", {"entities" : qUnion([Q0]), "operationType" : NewBodyOperationType.ADD, "depth" : 0.25 * mm});
        }
    });
